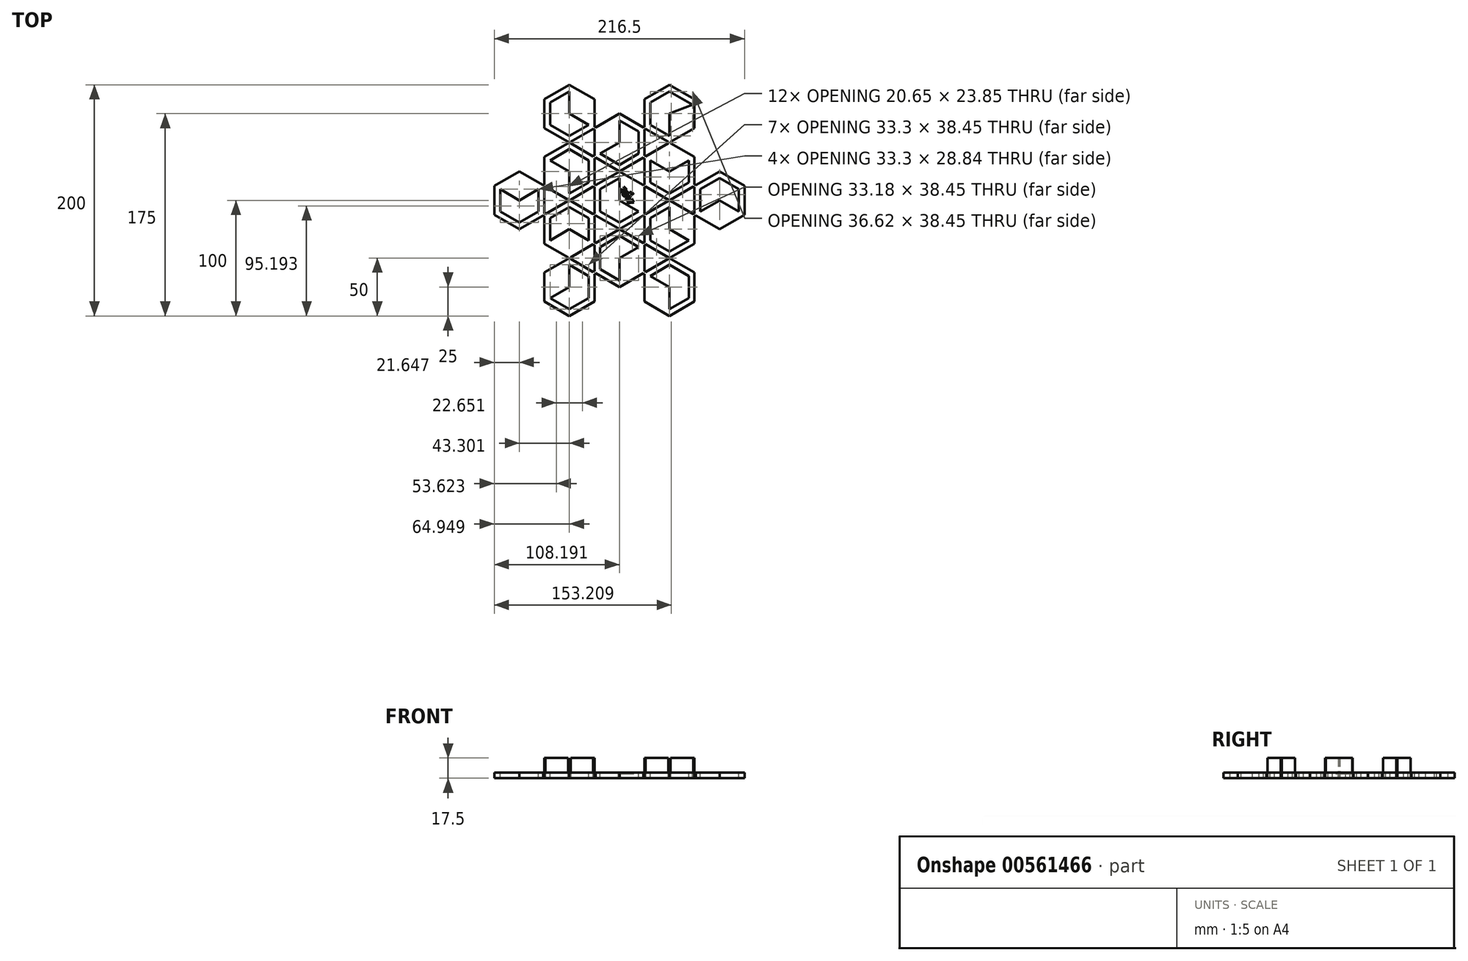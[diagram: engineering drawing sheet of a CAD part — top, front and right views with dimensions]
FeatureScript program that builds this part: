
annotation { "Feature Type Name" : "Feature", "Feature Type Description" : "" }
export const myFeature = defineFeature(function(context is Context, id is Id, definition is map)
    precondition{}
    {
        {
            var Q0;
            Q0=qCreatedBy(makeId("Top.planeOp"),FACE);
            var sketch = newSketch(context, id + "F0", { "sketchPlane" : qUnion([Q0])});
            skCircle(sketch, "E0.cCircle", {"center": v(0, 0) * mm, "radius": 25 * mm, "construction": true});
            skLineSegment(sketch, "E0.0", {"start": v(21.65, 12.5) * mm, "end": v(21.65, -12.5) * mm});
            skLineSegment(sketch, "E0.1", {"start": v(21.65, -12.5) * mm, "end": v(0, -25) * mm});
            skLineSegment(sketch, "E0.2", {"start": v(0, -25) * mm, "end": v(-21.65, -12.5) * mm});
            skLineSegment(sketch, "E0.3", {"start": v(-21.65, -12.5) * mm, "end": v(-21.65, 12.5) * mm});
            skLineSegment(sketch, "E0.4", {"start": v(-21.65, 12.5) * mm, "end": v(0, 25) * mm});
            skLineSegment(sketch, "E0.5", {"start": v(0, 25) * mm, "end": v(21.65, 12.5) * mm});
            skLineSegment(sketch, "E1.0", {"start": v(-16.65, 9.61) * mm, "end": v(0, 19.23) * mm});
            skLineSegment(sketch, "E1.1", {"start": v(-16.65, -9.61) * mm, "end": v(-16.65, 9.61) * mm});
            skLineSegment(sketch, "E1.2", {"start": v(0, -19.23) * mm, "end": v(-16.65, -9.61) * mm});
            skLineSegment(sketch, "E1.3", {"start": v(16.65, -9.61) * mm, "end": v(0, -19.23) * mm});
            skLineSegment(sketch, "E2", {"start": v(16.65, -9.61) * mm, "end": v(0, 0) * mm});
            skLineSegment(sketch, "E3", {"start": v(0, 19.23) * mm, "end": v(0, 0) * mm});
            skCircle(sketch, "E4.cCircle", {"center": v(0, -50) * mm, "radius": 25 * mm, "construction": true});
            skLineSegment(sketch, "E4.0", {"start": v(21.65, -62.5) * mm, "end": v(0, -75) * mm});
            skLineSegment(sketch, "E4.1", {"start": v(0, -75) * mm, "end": v(-21.65, -62.5) * mm});
            skLineSegment(sketch, "E4.2", {"start": v(-21.65, -62.5) * mm, "end": v(-21.65, -37.5) * mm});
            skLineSegment(sketch, "E4.3", {"start": v(-21.65, -37.5) * mm, "end": v(0, -25) * mm});
            skLineSegment(sketch, "E4.4", {"start": v(0, -25) * mm, "end": v(21.65, -37.5) * mm});
            skLineSegment(sketch, "E4.5", {"start": v(21.65, -37.5) * mm, "end": v(21.65, -62.5) * mm});
            skLineSegment(sketch, "E5.0", {"start": v(0, -30.77) * mm, "end": v(16.53, -40.32) * mm});
            skLineSegment(sketch, "E5.1", {"start": v(-16.65, -40.39) * mm, "end": v(0, -30.77) * mm});
            skLineSegment(sketch, "E5.2", {"start": v(-16.65, -59.61) * mm, "end": v(-16.65, -40.39) * mm});
            skLineSegment(sketch, "E5.3", {"start": v(0, -69.23) * mm, "end": v(-16.65, -59.61) * mm});
            skLineSegment(sketch, "E6", {"start": v(0, -69.23) * mm, "end": v(0, -50) * mm});
            skLineSegment(sketch, "E7", {"start": v(16.53, -40.32) * mm, "end": v(0, -50) * mm});
            skCircle(sketch, "E8.cCircle", {"center": v(-43.3, -25) * mm, "radius": 25 * mm, "construction": true});
            skLineSegment(sketch, "E8.0", {"start": v(-43.3, -50) * mm, "end": v(-64.95, -37.5) * mm});
            skLineSegment(sketch, "E8.1", {"start": v(-64.95, -37.5) * mm, "end": v(-64.95, -12.5) * mm});
            skLineSegment(sketch, "E8.2", {"start": v(-64.95, -12.5) * mm, "end": v(-43.3, 0) * mm});
            skLineSegment(sketch, "E8.3", {"start": v(-43.3, 0) * mm, "end": v(-21.65, -12.5) * mm});
            skLineSegment(sketch, "E8.4", {"start": v(-21.65, -12.5) * mm, "end": v(-21.65, -37.5) * mm});
            skLineSegment(sketch, "E8.5", {"start": v(-21.65, -37.5) * mm, "end": v(-43.3, -50) * mm});
            skLineSegment(sketch, "E9.0", {"start": v(-26.65, -15.39) * mm, "end": v(-26.65, -34.61) * mm});
            skLineSegment(sketch, "E9.1", {"start": v(-43.3, -5.77) * mm, "end": v(-26.65, -15.39) * mm});
            skLineSegment(sketch, "E9.2", {"start": v(-59.95, -15.39) * mm, "end": v(-43.3, -5.77) * mm});
            skLineSegment(sketch, "E9.3", {"start": v(-59.95, -34.61) * mm, "end": v(-59.95, -15.39) * mm});
            skLineSegment(sketch, "E10", {"start": v(-59.95, -34.61) * mm, "end": v(-43.3, -25) * mm});
            skLineSegment(sketch, "E11", {"start": v(-26.65, -34.61) * mm, "end": v(-43.3, -25) * mm});
            skCircle(sketch, "E12.cCircle", {"center": v(-43.3, 25) * mm, "radius": 25 * mm, "construction": true});
            skLineSegment(sketch, "E12.0", {"start": v(-64.95, 12.5) * mm, "end": v(-64.95, 37.5) * mm});
            skLineSegment(sketch, "E12.1", {"start": v(-64.95, 37.5) * mm, "end": v(-43.3, 50) * mm});
            skLineSegment(sketch, "E12.2", {"start": v(-43.3, 50) * mm, "end": v(-21.65, 37.5) * mm});
            skLineSegment(sketch, "E12.3", {"start": v(-21.65, 37.5) * mm, "end": v(-21.65, 12.5) * mm});
            skLineSegment(sketch, "E12.4", {"start": v(-21.65, 12.5) * mm, "end": v(-43.3, 0) * mm});
            skLineSegment(sketch, "E12.5", {"start": v(-43.3, 0) * mm, "end": v(-64.95, 12.5) * mm});
            skLineSegment(sketch, "E13.0", {"start": v(-26.65, 15.39) * mm, "end": v(-43.3, 5.77) * mm});
            skLineSegment(sketch, "E13.1", {"start": v(-26.65, 34.61) * mm, "end": v(-26.65, 15.39) * mm});
            skLineSegment(sketch, "E13.2", {"start": v(-43.3, 44.23) * mm, "end": v(-26.65, 34.61) * mm});
            skLineSegment(sketch, "E13.3", {"start": v(-59.95, 34.61) * mm, "end": v(-43.3, 44.23) * mm});
            skLineSegment(sketch, "E14", {"start": v(-59.95, 34.61) * mm, "end": v(-43.3, 25) * mm});
            skLineSegment(sketch, "E15", {"start": v(-43.3, 5.77) * mm, "end": v(-43.3, 25) * mm});
            skCircle(sketch, "E16.cCircle", {"center": v(0, 50) * mm, "radius": 25 * mm, "construction": true});
            skLineSegment(sketch, "E16.0", {"start": v(-21.65, 62.5) * mm, "end": v(0, 75) * mm});
            skLineSegment(sketch, "E16.1", {"start": v(0, 75) * mm, "end": v(21.65, 62.5) * mm});
            skLineSegment(sketch, "E16.2", {"start": v(21.65, 62.5) * mm, "end": v(21.65, 37.5) * mm});
            skLineSegment(sketch, "E16.3", {"start": v(21.65, 37.5) * mm, "end": v(0, 25) * mm});
            skLineSegment(sketch, "E16.4", {"start": v(0, 25) * mm, "end": v(-21.65, 37.5) * mm});
            skLineSegment(sketch, "E16.5", {"start": v(-21.65, 37.5) * mm, "end": v(-21.65, 62.5) * mm});
            skLineSegment(sketch, "E17.0", {"start": v(0, 30.77) * mm, "end": v(-16.65, 40.39) * mm});
            skLineSegment(sketch, "E17.1", {"start": v(16.65, 40.39) * mm, "end": v(0, 30.77) * mm});
            skLineSegment(sketch, "E17.2", {"start": v(16.65, 59.61) * mm, "end": v(16.65, 40.39) * mm});
            skLineSegment(sketch, "E17.3", {"start": v(0, 69.23) * mm, "end": v(16.65, 59.61) * mm});
            skLineSegment(sketch, "E18", {"start": v(0, 69.23) * mm, "end": v(0, 50) * mm});
            skLineSegment(sketch, "E19", {"start": v(-16.65, 40.39) * mm, "end": v(0, 50) * mm});
            skCircle(sketch, "E20.cCircle", {"center": v(43.3, 25) * mm, "radius": 25 * mm, "construction": true});
            skLineSegment(sketch, "E20.0", {"start": v(64.95, 12.5) * mm, "end": v(43.3, 0) * mm});
            skLineSegment(sketch, "E20.1", {"start": v(43.3, 0) * mm, "end": v(21.65, 12.5) * mm});
            skLineSegment(sketch, "E20.2", {"start": v(21.65, 12.5) * mm, "end": v(21.65, 37.5) * mm});
            skLineSegment(sketch, "E20.3", {"start": v(21.65, 37.5) * mm, "end": v(43.3, 50) * mm});
            skLineSegment(sketch, "E20.4", {"start": v(43.3, 50) * mm, "end": v(64.95, 37.5) * mm});
            skLineSegment(sketch, "E20.5", {"start": v(64.95, 37.5) * mm, "end": v(64.95, 12.5) * mm});
            skCircle(sketch, "E21.cCircle", {"center": v(43.3, -25) * mm, "radius": 25 * mm, "construction": true});
            skLineSegment(sketch, "E21.0", {"start": v(43.3, -50) * mm, "end": v(21.65, -37.5) * mm});
            skLineSegment(sketch, "E21.1", {"start": v(21.65, -37.5) * mm, "end": v(21.65, -12.5) * mm});
            skLineSegment(sketch, "E21.2", {"start": v(21.65, -12.5) * mm, "end": v(43.3, 0) * mm});
            skLineSegment(sketch, "E21.3", {"start": v(43.3, 0) * mm, "end": v(64.95, -12.5) * mm});
            skLineSegment(sketch, "E21.4", {"start": v(64.95, -12.5) * mm, "end": v(64.95, -37.5) * mm});
            skLineSegment(sketch, "E21.5", {"start": v(64.95, -37.5) * mm, "end": v(43.3, -50) * mm});
            skCircle(sketch, "E22.cCircle", {"center": v(-86.6, 0) * mm, "radius": 25 * mm, "construction": true});
            skLineSegment(sketch, "E22.0", {"start": v(-86.6, 25) * mm, "end": v(-64.95, 12.5) * mm});
            skLineSegment(sketch, "E22.1", {"start": v(-64.95, 12.5) * mm, "end": v(-64.95, -12.5) * mm});
            skLineSegment(sketch, "E22.2", {"start": v(-64.95, -12.5) * mm, "end": v(-86.6, -25) * mm});
            skLineSegment(sketch, "E22.3", {"start": v(-86.6, -25) * mm, "end": v(-108.25, -12.5) * mm});
            skLineSegment(sketch, "E22.4", {"start": v(-108.25, -12.5) * mm, "end": v(-108.25, 12.5) * mm});
            skLineSegment(sketch, "E22.5", {"start": v(-108.25, 12.5) * mm, "end": v(-86.6, 25) * mm});
            skLineSegment(sketch, "E23.0", {"start": v(-103.25, -9.61) * mm, "end": v(-103.25, 9.61) * mm});
            skLineSegment(sketch, "E23.1", {"start": v(-86.6, -19.23) * mm, "end": v(-103.25, -9.61) * mm});
            skLineSegment(sketch, "E23.2", {"start": v(-69.95, -9.61) * mm, "end": v(-86.6, -19.23) * mm});
            skLineSegment(sketch, "E23.3", {"start": v(-69.95, 9.61) * mm, "end": v(-69.95, -9.61) * mm});
            skLineSegment(sketch, "E24", {"start": v(-69.95, 9.61) * mm, "end": v(-86.6, 0) * mm});
            skLineSegment(sketch, "E25", {"start": v(-103.25, 9.61) * mm, "end": v(-86.6, 0) * mm});
            skCircle(sketch, "E26.cCircle", {"center": v(-43.3, 75) * mm, "radius": 25 * mm, "construction": true});
            skLineSegment(sketch, "E26.0", {"start": v(-21.65, 87.5) * mm, "end": v(-21.65, 62.5) * mm});
            skLineSegment(sketch, "E26.1", {"start": v(-21.65, 62.5) * mm, "end": v(-43.3, 50) * mm});
            skLineSegment(sketch, "E26.2", {"start": v(-43.3, 50) * mm, "end": v(-64.95, 62.5) * mm});
            skLineSegment(sketch, "E26.3", {"start": v(-64.95, 62.5) * mm, "end": v(-64.95, 87.5) * mm});
            skLineSegment(sketch, "E26.4", {"start": v(-64.95, 87.5) * mm, "end": v(-43.3, 100) * mm});
            skLineSegment(sketch, "E26.5", {"start": v(-43.3, 100) * mm, "end": v(-21.65, 87.5) * mm});
            skLineSegment(sketch, "E27.0", {"start": v(-59.95, 84.61) * mm, "end": v(-43.3, 94.23) * mm});
            skLineSegment(sketch, "E27.1", {"start": v(-59.95, 65.39) * mm, "end": v(-59.95, 84.61) * mm});
            skLineSegment(sketch, "E27.2", {"start": v(-43.3, 55.77) * mm, "end": v(-59.95, 65.39) * mm});
            skLineSegment(sketch, "E27.3", {"start": v(-26.65, 65.39) * mm, "end": v(-43.3, 55.77) * mm});
            skLineSegment(sketch, "E28", {"start": v(-26.65, 65.39) * mm, "end": v(-43.3, 75) * mm});
            skLineSegment(sketch, "E29", {"start": v(-43.3, 94.23) * mm, "end": v(-43.3, 75) * mm});
            skCircle(sketch, "E30.cCircle", {"center": v(43.3, 75) * mm, "radius": 25 * mm, "construction": true});
            skLineSegment(sketch, "E30.0", {"start": v(64.95, 62.5) * mm, "end": v(43.3, 50) * mm});
            skLineSegment(sketch, "E30.1", {"start": v(43.3, 50) * mm, "end": v(21.65, 62.5) * mm});
            skLineSegment(sketch, "E30.2", {"start": v(21.65, 62.5) * mm, "end": v(21.65, 87.5) * mm});
            skLineSegment(sketch, "E30.3", {"start": v(21.65, 87.5) * mm, "end": v(43.3, 100) * mm});
            skLineSegment(sketch, "E30.4", {"start": v(43.3, 100) * mm, "end": v(64.95, 87.5) * mm});
            skLineSegment(sketch, "E30.5", {"start": v(64.95, 87.5) * mm, "end": v(64.95, 62.5) * mm});
            skLineSegment(sketch, "E31.0", {"start": v(43.3, 94.23) * mm, "end": v(63.27, 82.7) * mm});
            skLineSegment(sketch, "E31.1", {"start": v(26.65, 84.61) * mm, "end": v(43.3, 94.23) * mm});
            skLineSegment(sketch, "E31.2", {"start": v(26.65, 65.39) * mm, "end": v(26.65, 84.61) * mm});
            skLineSegment(sketch, "E31.3", {"start": v(43.3, 55.77) * mm, "end": v(26.65, 65.39) * mm});
            skLineSegment(sketch, "E32", {"start": v(43.3, 55.77) * mm, "end": v(43.3, 75) * mm});
            skLineSegment(sketch, "E33", {"start": v(63.27, 82.7) * mm, "end": v(43.3, 75) * mm});
            skCircle(sketch, "E34.cCircle", {"center": v(86.6, 0) * mm, "radius": 25 * mm, "construction": true});
            skLineSegment(sketch, "E34.0", {"start": v(86.6, -25) * mm, "end": v(64.95, -12.5) * mm});
            skLineSegment(sketch, "E34.1", {"start": v(64.95, -12.5) * mm, "end": v(64.95, 12.5) * mm});
            skLineSegment(sketch, "E34.2", {"start": v(64.95, 12.5) * mm, "end": v(86.6, 25) * mm});
            skLineSegment(sketch, "E34.3", {"start": v(86.6, 25) * mm, "end": v(108.25, 12.5) * mm});
            skLineSegment(sketch, "E34.4", {"start": v(108.25, 12.5) * mm, "end": v(108.25, -12.5) * mm});
            skLineSegment(sketch, "E34.5", {"start": v(108.25, -12.5) * mm, "end": v(86.6, -25) * mm});
            skLineSegment(sketch, "E35.0", {"start": v(103.25, 9.61) * mm, "end": v(103.25, -9.61) * mm});
            skLineSegment(sketch, "E35.1", {"start": v(86.6, 19.23) * mm, "end": v(103.25, 9.61) * mm});
            skLineSegment(sketch, "E35.2", {"start": v(69.95, 9.61) * mm, "end": v(86.6, 19.23) * mm});
            skLineSegment(sketch, "E35.3", {"start": v(69.95, -9.61) * mm, "end": v(69.95, 9.61) * mm});
            skLineSegment(sketch, "E36", {"start": v(69.95, -9.61) * mm, "end": v(86.6, 0) * mm});
            skLineSegment(sketch, "E37", {"start": v(103.25, -9.61) * mm, "end": v(86.6, 0) * mm});
            skCircle(sketch, "E38.cCircle", {"center": v(43.3, -75) * mm, "radius": 25 * mm, "construction": true});
            skLineSegment(sketch, "E38.0", {"start": v(21.65, -87.5) * mm, "end": v(21.65, -62.5) * mm});
            skLineSegment(sketch, "E38.1", {"start": v(21.65, -62.5) * mm, "end": v(43.3, -50) * mm});
            skLineSegment(sketch, "E38.2", {"start": v(43.3, -50) * mm, "end": v(64.95, -62.5) * mm});
            skLineSegment(sketch, "E38.3", {"start": v(64.95, -62.5) * mm, "end": v(64.95, -87.5) * mm});
            skLineSegment(sketch, "E38.4", {"start": v(64.95, -87.5) * mm, "end": v(43.3, -100) * mm});
            skLineSegment(sketch, "E38.5", {"start": v(43.3, -100) * mm, "end": v(21.65, -87.5) * mm});
            skLineSegment(sketch, "E39.0", {"start": v(59.95, -84.61) * mm, "end": v(43.3, -94.23) * mm});
            skLineSegment(sketch, "E39.1", {"start": v(59.95, -65.39) * mm, "end": v(59.95, -84.61) * mm});
            skLineSegment(sketch, "E39.2", {"start": v(43.3, -55.77) * mm, "end": v(59.95, -65.39) * mm});
            skLineSegment(sketch, "E39.3", {"start": v(26.65, -65.39) * mm, "end": v(43.3, -55.77) * mm});
            skLineSegment(sketch, "E40", {"start": v(26.65, -65.39) * mm, "end": v(43.3, -75) * mm});
            skLineSegment(sketch, "E41", {"start": v(43.3, -94.23) * mm, "end": v(43.3, -75) * mm});
            skCircle(sketch, "E42.cCircle", {"center": v(-43.3, -75) * mm, "radius": 25 * mm, "construction": true});
            skLineSegment(sketch, "E42.0", {"start": v(-64.95, -62.5) * mm, "end": v(-43.3, -50) * mm});
            skLineSegment(sketch, "E42.1", {"start": v(-43.3, -50) * mm, "end": v(-21.65, -62.5) * mm});
            skLineSegment(sketch, "E42.2", {"start": v(-21.65, -62.5) * mm, "end": v(-21.65, -87.5) * mm});
            skLineSegment(sketch, "E42.3", {"start": v(-21.65, -87.5) * mm, "end": v(-43.3, -100) * mm});
            skLineSegment(sketch, "E42.4", {"start": v(-43.3, -100) * mm, "end": v(-64.95, -87.5) * mm});
            skLineSegment(sketch, "E42.5", {"start": v(-64.95, -87.5) * mm, "end": v(-64.95, -62.5) * mm});
            skLineSegment(sketch, "E43.0", {"start": v(-43.3, -94.23) * mm, "end": v(-59.95, -84.61) * mm});
            skLineSegment(sketch, "E43.1", {"start": v(-26.65, -84.61) * mm, "end": v(-43.3, -94.23) * mm});
            skLineSegment(sketch, "E43.2", {"start": v(-26.65, -65.39) * mm, "end": v(-26.65, -84.61) * mm});
            skLineSegment(sketch, "E43.3", {"start": v(-43.3, -55.77) * mm, "end": v(-26.65, -65.39) * mm});
            skLineSegment(sketch, "E44", {"start": v(-43.3, -55.77) * mm, "end": v(-43.3, -75) * mm});
            skLineSegment(sketch, "E45", {"start": v(-59.95, -84.61) * mm, "end": v(-43.3, -75) * mm});
            skLineSegment(sketch, "E46.bottom", {"start": v(-20.65, -11.5) * mm, "end": v(-22.65, -11.5) * mm});
            skLineSegment(sketch, "E46.top", {"start": v(-20.65, -13.5) * mm, "end": v(-22.65, -13.5) * mm});
            skLineSegment(sketch, "E46.left", {"start": v(-20.65, -11.5) * mm, "end": v(-20.65, -13.5) * mm});
            skLineSegment(sketch, "E46.right", {"start": v(-22.65, -11.5) * mm, "end": v(-22.65, -13.5) * mm});
            skPoint(sketch, "E46.middle", {"position": v(-21.65, -12.5) * mm});
            skLineSegment(sketch, "E47.bottom", {"start": v(1, -24) * mm, "end": v(-1, -24) * mm});
            skLineSegment(sketch, "E47.top", {"start": v(1, -26) * mm, "end": v(-1, -26) * mm});
            skLineSegment(sketch, "E47.left", {"start": v(1, -24) * mm, "end": v(1, -26) * mm});
            skLineSegment(sketch, "E47.right", {"start": v(-1, -24) * mm, "end": v(-1, -26) * mm});
            skPoint(sketch, "E47.middle", {"position": v(0, -25) * mm});
            skLineSegment(sketch, "E48.bottom", {"start": v(20.65, -11.5) * mm, "end": v(22.65, -11.5) * mm});
            skLineSegment(sketch, "E48.top", {"start": v(20.65, -13.5) * mm, "end": v(22.65, -13.5) * mm});
            skLineSegment(sketch, "E48.left", {"start": v(20.65, -11.5) * mm, "end": v(20.65, -13.5) * mm});
            skLineSegment(sketch, "E48.right", {"start": v(22.65, -11.5) * mm, "end": v(22.65, -13.5) * mm});
            skPoint(sketch, "E48.middle", {"position": v(21.65, -12.5) * mm});
            skLineSegment(sketch, "E49.bottom", {"start": v(20.65, 11.5) * mm, "end": v(22.65, 11.5) * mm});
            skLineSegment(sketch, "E49.top", {"start": v(20.65, 13.5) * mm, "end": v(22.65, 13.5) * mm});
            skLineSegment(sketch, "E49.left", {"start": v(20.65, 11.5) * mm, "end": v(20.65, 13.5) * mm});
            skLineSegment(sketch, "E49.right", {"start": v(22.65, 11.5) * mm, "end": v(22.65, 13.5) * mm});
            skPoint(sketch, "E49.middle", {"position": v(21.65, 12.5) * mm});
            skLineSegment(sketch, "E50.bottom", {"start": v(-1, 24) * mm, "end": v(1, 24) * mm});
            skLineSegment(sketch, "E50.top", {"start": v(-1, 26) * mm, "end": v(1, 26) * mm});
            skLineSegment(sketch, "E50.left", {"start": v(-1, 24) * mm, "end": v(-1, 26) * mm});
            skLineSegment(sketch, "E50.right", {"start": v(1, 24) * mm, "end": v(1, 26) * mm});
            skPoint(sketch, "E50.middle", {"position": v(0, 25) * mm});
            skLineSegment(sketch, "E51.bottom", {"start": v(-20.65, 11.5) * mm, "end": v(-22.65, 11.5) * mm});
            skLineSegment(sketch, "E51.top", {"start": v(-20.65, 13.5) * mm, "end": v(-22.65, 13.5) * mm});
            skLineSegment(sketch, "E51.left", {"start": v(-20.65, 11.5) * mm, "end": v(-20.65, 13.5) * mm});
            skLineSegment(sketch, "E51.right", {"start": v(-22.65, 11.5) * mm, "end": v(-22.65, 13.5) * mm});
            skPoint(sketch, "E51.middle", {"position": v(-21.65, 12.5) * mm});
            skLineSegment(sketch, "E52.bottom", {"start": v(44.3, -1) * mm, "end": v(42.3, -1) * mm});
            skLineSegment(sketch, "E52.top", {"start": v(44.3, 1) * mm, "end": v(42.3, 1) * mm});
            skLineSegment(sketch, "E52.left", {"start": v(44.3, -1) * mm, "end": v(44.3, 1) * mm});
            skLineSegment(sketch, "E52.right", {"start": v(42.3, -1) * mm, "end": v(42.3, 1) * mm});
            skPoint(sketch, "E52.middle", {"position": v(43.3, 0) * mm});
            skLineSegment(sketch, "E53.bottom", {"start": v(20.65, 38.5) * mm, "end": v(22.65, 38.5) * mm});
            skLineSegment(sketch, "E53.top", {"start": v(20.65, 36.5) * mm, "end": v(22.65, 36.5) * mm});
            skLineSegment(sketch, "E53.left", {"start": v(20.65, 38.5) * mm, "end": v(20.65, 36.5) * mm});
            skLineSegment(sketch, "E53.right", {"start": v(22.65, 38.5) * mm, "end": v(22.65, 36.5) * mm});
            skPoint(sketch, "E53.middle", {"position": v(21.65, 37.5) * mm});
            skLineSegment(sketch, "E54.bottom", {"start": v(63.95, 13.5) * mm, "end": v(65.95, 13.5) * mm});
            skLineSegment(sketch, "E54.top", {"start": v(63.95, 11.5) * mm, "end": v(65.95, 11.5) * mm});
            skLineSegment(sketch, "E54.left", {"start": v(63.95, 13.5) * mm, "end": v(63.95, 11.5) * mm});
            skLineSegment(sketch, "E54.right", {"start": v(65.95, 13.5) * mm, "end": v(65.95, 11.5) * mm});
            skPoint(sketch, "E54.middle", {"position": v(64.95, 12.5) * mm});
            skLineSegment(sketch, "E55.bottom", {"start": v(-20.65, 38.5) * mm, "end": v(-22.65, 38.5) * mm});
            skLineSegment(sketch, "E55.top", {"start": v(-20.65, 36.5) * mm, "end": v(-22.65, 36.5) * mm});
            skLineSegment(sketch, "E55.left", {"start": v(-20.65, 38.5) * mm, "end": v(-20.65, 36.5) * mm});
            skLineSegment(sketch, "E55.right", {"start": v(-22.65, 38.5) * mm, "end": v(-22.65, 36.5) * mm});
            skPoint(sketch, "E55.middle", {"position": v(-21.65, 37.5) * mm});
            skLineSegment(sketch, "E56.bottom", {"start": v(-42.3, 1) * mm, "end": v(-44.3, 1) * mm});
            skLineSegment(sketch, "E56.top", {"start": v(-42.3, -1) * mm, "end": v(-44.3, -1) * mm});
            skLineSegment(sketch, "E56.left", {"start": v(-42.3, 1) * mm, "end": v(-42.3, -1) * mm});
            skLineSegment(sketch, "E56.right", {"start": v(-44.3, 1) * mm, "end": v(-44.3, -1) * mm});
            skPoint(sketch, "E56.middle", {"position": v(-43.3, 0) * mm});
            skLineSegment(sketch, "E57.bottom", {"start": v(65.95, -11.5) * mm, "end": v(63.95, -11.5) * mm});
            skLineSegment(sketch, "E57.top", {"start": v(65.95, -13.5) * mm, "end": v(63.95, -13.5) * mm});
            skLineSegment(sketch, "E57.left", {"start": v(65.95, -11.5) * mm, "end": v(65.95, -13.5) * mm});
            skLineSegment(sketch, "E57.right", {"start": v(63.95, -11.5) * mm, "end": v(63.95, -13.5) * mm});
            skPoint(sketch, "E57.middle", {"position": v(64.95, -12.5) * mm});
            skLineSegment(sketch, "E58.bottom", {"start": v(44.3, -49) * mm, "end": v(42.3, -49) * mm});
            skLineSegment(sketch, "E58.top", {"start": v(44.3, -51) * mm, "end": v(42.3, -51) * mm});
            skLineSegment(sketch, "E58.left", {"start": v(44.3, -49) * mm, "end": v(44.3, -51) * mm});
            skLineSegment(sketch, "E58.right", {"start": v(42.3, -49) * mm, "end": v(42.3, -51) * mm});
            skPoint(sketch, "E58.middle", {"position": v(43.3, -50) * mm});
            skLineSegment(sketch, "E59.bottom", {"start": v(-42.3, -49) * mm, "end": v(-44.3, -49) * mm});
            skLineSegment(sketch, "E59.top", {"start": v(-42.3, -51) * mm, "end": v(-44.3, -51) * mm});
            skLineSegment(sketch, "E59.left", {"start": v(-42.3, -49) * mm, "end": v(-42.3, -51) * mm});
            skLineSegment(sketch, "E59.right", {"start": v(-44.3, -49) * mm, "end": v(-44.3, -51) * mm});
            skPoint(sketch, "E59.middle", {"position": v(-43.3, -50) * mm});
            skLineSegment(sketch, "E60.bottom", {"start": v(-63.95, -13.5) * mm, "end": v(-65.95, -13.5) * mm});
            skLineSegment(sketch, "E60.top", {"start": v(-63.95, -11.5) * mm, "end": v(-65.95, -11.5) * mm});
            skLineSegment(sketch, "E60.left", {"start": v(-63.95, -13.5) * mm, "end": v(-63.95, -11.5) * mm});
            skLineSegment(sketch, "E60.right", {"start": v(-65.95, -13.5) * mm, "end": v(-65.95, -11.5) * mm});
            skPoint(sketch, "E60.middle", {"position": v(-64.95, -12.5) * mm});
            skLineSegment(sketch, "E61.bottom", {"start": v(-63.95, 13.5) * mm, "end": v(-65.95, 13.5) * mm});
            skLineSegment(sketch, "E61.top", {"start": v(-63.95, 11.5) * mm, "end": v(-65.95, 11.5) * mm});
            skLineSegment(sketch, "E61.left", {"start": v(-63.95, 13.5) * mm, "end": v(-63.95, 11.5) * mm});
            skLineSegment(sketch, "E61.right", {"start": v(-65.95, 13.5) * mm, "end": v(-65.95, 11.5) * mm});
            skPoint(sketch, "E61.middle", {"position": v(-64.95, 12.5) * mm});
            skLineSegment(sketch, "E62.bottom", {"start": v(-42.3, 51) * mm, "end": v(-44.3, 51) * mm});
            skLineSegment(sketch, "E62.top", {"start": v(-42.3, 49) * mm, "end": v(-44.3, 49) * mm});
            skLineSegment(sketch, "E62.left", {"start": v(-42.3, 51) * mm, "end": v(-42.3, 49) * mm});
            skLineSegment(sketch, "E62.right", {"start": v(-44.3, 51) * mm, "end": v(-44.3, 49) * mm});
            skPoint(sketch, "E62.middle", {"position": v(-43.3, 50) * mm});
            skLineSegment(sketch, "E63.bottom", {"start": v(-22.65, 63.5) * mm, "end": v(-20.65, 63.5) * mm});
            skLineSegment(sketch, "E63.top", {"start": v(-22.65, 61.5) * mm, "end": v(-20.65, 61.5) * mm});
            skLineSegment(sketch, "E63.left", {"start": v(-22.65, 63.5) * mm, "end": v(-22.65, 61.5) * mm});
            skLineSegment(sketch, "E63.right", {"start": v(-20.65, 63.5) * mm, "end": v(-20.65, 61.5) * mm});
            skPoint(sketch, "E63.middle", {"position": v(-21.65, 62.5) * mm});
            skLineSegment(sketch, "E64.bottom", {"start": v(22.65, 63.5) * mm, "end": v(20.65, 63.5) * mm});
            skLineSegment(sketch, "E64.top", {"start": v(22.65, 61.5) * mm, "end": v(20.65, 61.5) * mm});
            skLineSegment(sketch, "E64.left", {"start": v(22.65, 63.5) * mm, "end": v(22.65, 61.5) * mm});
            skLineSegment(sketch, "E64.right", {"start": v(20.65, 63.5) * mm, "end": v(20.65, 61.5) * mm});
            skPoint(sketch, "E64.middle", {"position": v(21.65, 62.5) * mm});
            skLineSegment(sketch, "E65.bottom", {"start": v(44.3, 51) * mm, "end": v(42.3, 51) * mm});
            skLineSegment(sketch, "E65.top", {"start": v(44.3, 49) * mm, "end": v(42.3, 49) * mm});
            skLineSegment(sketch, "E65.left", {"start": v(44.3, 51) * mm, "end": v(44.3, 49) * mm});
            skLineSegment(sketch, "E65.right", {"start": v(42.3, 51) * mm, "end": v(42.3, 49) * mm});
            skPoint(sketch, "E65.middle", {"position": v(43.3, 50) * mm});
            skLineSegment(sketch, "E66.bottom", {"start": v(-20.65, -61.5) * mm, "end": v(-22.65, -61.5) * mm});
            skLineSegment(sketch, "E66.top", {"start": v(-20.65, -63.5) * mm, "end": v(-22.65, -63.5) * mm});
            skLineSegment(sketch, "E66.left", {"start": v(-20.65, -61.5) * mm, "end": v(-20.65, -63.5) * mm});
            skLineSegment(sketch, "E66.right", {"start": v(-22.65, -61.5) * mm, "end": v(-22.65, -63.5) * mm});
            skPoint(sketch, "E66.middle", {"position": v(-21.65, -62.5) * mm});
            skLineSegment(sketch, "E67.bottom", {"start": v(-22.65, -36.5) * mm, "end": v(-20.65, -36.5) * mm});
            skLineSegment(sketch, "E67.top", {"start": v(-22.65, -38.5) * mm, "end": v(-20.65, -38.5) * mm});
            skLineSegment(sketch, "E67.left", {"start": v(-22.65, -36.5) * mm, "end": v(-22.65, -38.5) * mm});
            skLineSegment(sketch, "E67.right", {"start": v(-20.65, -36.5) * mm, "end": v(-20.65, -38.5) * mm});
            skPoint(sketch, "E67.middle", {"position": v(-21.65, -37.5) * mm});
            skLineSegment(sketch, "E68.bottom", {"start": v(22.65, -36.5) * mm, "end": v(20.65, -36.5) * mm});
            skLineSegment(sketch, "E68.top", {"start": v(22.65, -38.5) * mm, "end": v(20.65, -38.5) * mm});
            skLineSegment(sketch, "E68.left", {"start": v(22.65, -36.5) * mm, "end": v(22.65, -38.5) * mm});
            skLineSegment(sketch, "E68.right", {"start": v(20.65, -36.5) * mm, "end": v(20.65, -38.5) * mm});
            skPoint(sketch, "E68.middle", {"position": v(21.65, -37.5) * mm});
            skLineSegment(sketch, "E69.bottom", {"start": v(20.65, -61.5) * mm, "end": v(22.65, -61.5) * mm});
            skLineSegment(sketch, "E69.top", {"start": v(20.65, -63.5) * mm, "end": v(22.65, -63.5) * mm});
            skLineSegment(sketch, "E69.left", {"start": v(20.65, -61.5) * mm, "end": v(20.65, -63.5) * mm});
            skLineSegment(sketch, "E69.right", {"start": v(22.65, -61.5) * mm, "end": v(22.65, -63.5) * mm});
            skPoint(sketch, "E69.middle", {"position": v(21.65, -62.5) * mm});
            skLineSegment(sketch, "E70.0", {"start": v(26.65, -15.39) * mm, "end": v(43.3, -5.77) * mm});
            skLineSegment(sketch, "E70.1", {"start": v(26.65, -34.61) * mm, "end": v(26.65, -15.39) * mm});
            skLineSegment(sketch, "E70.2", {"start": v(43.3, -44.23) * mm, "end": v(26.65, -34.61) * mm});
            skLineSegment(sketch, "E70.3", {"start": v(59.95, -34.61) * mm, "end": v(43.3, -44.23) * mm});
            skPoint(sketch, "E71.endSnap0", {"position": v(43.3, -1) * mm});
            skLineSegment(sketch, "E72", {"start": v(59.95, -34.61) * mm, "end": v(43.3, -25) * mm});
            skLineSegment(sketch, "E73", {"start": v(43.3, -5.77) * mm, "end": v(43.3, -25) * mm});
            skLineSegment(sketch, "E74.0", {"start": v(26.65, 15.39) * mm, "end": v(26.65, 34.61) * mm});
            skLineSegment(sketch, "E74.1", {"start": v(43.3, 5.77) * mm, "end": v(26.65, 15.39) * mm});
            skLineSegment(sketch, "E74.2", {"start": v(59.95, 15.39) * mm, "end": v(43.3, 5.77) * mm});
            skLineSegment(sketch, "E74.3", {"start": v(59.95, 34.61) * mm, "end": v(59.95, 15.39) * mm});
            skLineSegment(sketch, "E75", {"start": v(59.95, 34.61) * mm, "end": v(43.3, 25) * mm});
            skLineSegment(sketch, "E76.trimOffspring", {"start": v(26.65, 34.61) * mm, "end": v(43.3, 25) * mm});
            skSolve(sketch);
        }
        {
            var Q0;
            Q0=makeQuery(id+"F0.imprint","IMPRINT",FACE,{"disambiguationData":[TD([[makeQuery(id+"F0.imprint","IMPRINT",EDGE,{"derivedFrom":sQuery(id+"F0.wireOp",EDGE,"E13.0")}),1.0]])]});
            var Q1;
            {var subQ1=sQuery(id+"F0.wireOp",EDGE,"E62.top");Q1=makeQuery(id+"F0.imprint","IMPRINT",FACE,{"disambiguationData":[TD([[makeQuery(id+"F0.imprint","IMPRINT",EDGE,{"derivedFrom":subQ1}),-1.0]])]});}
            var Q2;
            {var subQ1=sQuery(id+"F0.wireOp",EDGE,"E12.1");var subQ3=sQuery(id+"F0.wireOp",EDGE,"E62.right");var subQ4=makeQuery(id+"F0.imprint","INTERSECT",VERTEX,{"derivedFrom":[subQ1,subQ3]});Q2=makeQuery(id+"F0.imprint","IMPRINT",FACE,{"disambiguationData":[TD([[makeQuery(id+"F0.imprint","IMPRINT",EDGE,{"disambiguationData":[TD([[subQ4,1.0]])],"derivedFrom":subQ3}),1.0]])]});}
            var Q3;
            {var subQ0=sQuery(id+"F0.wireOp",EDGE,"E62.bottom");Q3=makeQuery(id+"F0.imprint","IMPRINT",FACE,{"disambiguationData":[TD([[makeQuery(id+"F0.imprint","IMPRINT",EDGE,{"derivedFrom":subQ0}),1.0]])]});}
            var Q4;
            {var subQ1=sQuery(id+"F0.wireOp",EDGE,"E12.2");var subQ3=sQuery(id+"F0.wireOp",EDGE,"E62.left");var subQ4=makeQuery(id+"F0.imprint","INTERSECT",VERTEX,{"derivedFrom":[subQ1,subQ3]});Q4=makeQuery(id+"F0.imprint","IMPRINT",FACE,{"disambiguationData":[TD([[makeQuery(id+"F0.imprint","IMPRINT",EDGE,{"disambiguationData":[TD([[subQ4,1.0]])],"derivedFrom":subQ3}),-1.0]])]});}
            var Q5;
            {var subQ11=sQuery(id+"F0.wireOp",EDGE,"E26.3");Q5=makeQuery(id+"F0.imprint","IMPRINT",FACE,{"disambiguationData":[TD([[makeQuery(id+"F0.imprint","IMPRINT",EDGE,{"derivedFrom":subQ11}),-1.0]])]});}
            var Q6;
            {var subQ3=sQuery(id+"F0.wireOp",EDGE,"E55.left");var subQ5=sQuery(id+"F0.wireOp",EDGE,"E55.bottom");var subQ7=makeQuery(id+"F0.imprint","INTERSECT",VERTEX,{"derivedFrom":[subQ5,subQ3]});Q6=makeQuery(id+"F0.imprint","IMPRINT",FACE,{"disambiguationData":[TD([[makeQuery(id+"F0.imprint","IMPRINT",EDGE,{"disambiguationData":[TD([[subQ7,-1.0]])],"derivedFrom":subQ5}),1.0]])]});}
            var Q7;
            Q7=makeQuery(id+"F0.imprint","IMPRINT",FACE,{"disambiguationData":[TD([[makeQuery(id+"F0.imprint","IMPRINT",EDGE,{"derivedFrom":sQuery(id+"F0.wireOp",EDGE,"E17.0")}),1.0]])]});
            var Q8;
            {var subQ3=sQuery(id+"F0.wireOp",EDGE,"E55.right");var subQ5=sQuery(id+"F0.wireOp",EDGE,"E55.top");var subQ7=makeQuery(id+"F0.imprint","INTERSECT",VERTEX,{"derivedFrom":[subQ5,subQ3]});Q8=makeQuery(id+"F0.imprint","IMPRINT",FACE,{"disambiguationData":[TD([[makeQuery(id+"F0.imprint","IMPRINT",EDGE,{"disambiguationData":[TD([[subQ7,1.0]])],"derivedFrom":subQ5}),-1.0]])]});}
            var Q9;
            {var subQ3=sQuery(id+"F0.wireOp",EDGE,"E55.top");var subQ5=sQuery(id+"F0.wireOp",EDGE,"E55.left");var subQ7=makeQuery(id+"F0.imprint","INTERSECT",VERTEX,{"derivedFrom":[subQ3,subQ5]});Q9=makeQuery(id+"F0.imprint","IMPRINT",FACE,{"disambiguationData":[TD([[makeQuery(id+"F0.imprint","IMPRINT",EDGE,{"disambiguationData":[TD([[subQ7,-1.0]])],"derivedFrom":subQ3}),-1.0]])]});}
            var Q10;
            {var subQ3=sQuery(id+"F0.wireOp",EDGE,"E55.right");var subQ5=sQuery(id+"F0.wireOp",EDGE,"E55.bottom");var subQ7=makeQuery(id+"F0.imprint","INTERSECT",VERTEX,{"derivedFrom":[subQ5,subQ3]});Q10=makeQuery(id+"F0.imprint","IMPRINT",FACE,{"disambiguationData":[TD([[makeQuery(id+"F0.imprint","IMPRINT",EDGE,{"disambiguationData":[TD([[subQ7,1.0]])],"derivedFrom":subQ5}),1.0]])]});}
            var Q11;
            Q11=makeQuery(id+"F0.imprint","IMPRINT",FACE,{"disambiguationData":[TD([[makeQuery(id+"F0.imprint","IMPRINT",EDGE,{"derivedFrom":sQuery(id+"F0.wireOp",EDGE,"E1.0")}),1.0]])]});
            var Q12;
            {var subQ1=sQuery(id+"F0.wireOp",EDGE,"E50.top");Q12=makeQuery(id+"F0.imprint","IMPRINT",FACE,{"disambiguationData":[TD([[makeQuery(id+"F0.imprint","IMPRINT",EDGE,{"derivedFrom":subQ1}),-1.0]])]});}
            var Q13;
            {var subQ1=sQuery(id+"F0.wireOp",EDGE,"E50.bottom");Q13=makeQuery(id+"F0.imprint","IMPRINT",FACE,{"disambiguationData":[TD([[makeQuery(id+"F0.imprint","IMPRINT",EDGE,{"derivedFrom":subQ1}),1.0]])]});}
            var Q14;
            {var subQ1=sQuery(id+"F0.wireOp",EDGE,"E50.bottom");Q14=makeQuery(id+"F0.imprint","IMPRINT",FACE,{"disambiguationData":[TD([[makeQuery(id+"F0.imprint","IMPRINT",EDGE,{"derivedFrom":subQ1}),1.0]])]});}
            var Q15;
            {var subQ1=sQuery(id+"F0.wireOp",EDGE,"E0.4");var subQ3=sQuery(id+"F0.wireOp",EDGE,"E50.left");var subQ4=makeQuery(id+"F0.imprint","INTERSECT",VERTEX,{"derivedFrom":[subQ1,subQ3]});Q15=makeQuery(id+"F0.imprint","IMPRINT",FACE,{"disambiguationData":[TD([[makeQuery(id+"F0.imprint","IMPRINT",EDGE,{"disambiguationData":[TD([[subQ4,-1.0]])],"derivedFrom":subQ3}),-1.0]])]});}
            var Q16;
            {var subQ1=sQuery(id+"F0.wireOp",EDGE,"E0.5");var subQ3=sQuery(id+"F0.wireOp",EDGE,"E50.right");var subQ4=makeQuery(id+"F0.imprint","INTERSECT",VERTEX,{"derivedFrom":[subQ1,subQ3]});Q16=makeQuery(id+"F0.imprint","IMPRINT",FACE,{"disambiguationData":[TD([[makeQuery(id+"F0.imprint","IMPRINT",EDGE,{"disambiguationData":[TD([[subQ4,-1.0]])],"derivedFrom":subQ3}),1.0]])]});}
            var Q17;
            {var subQ3=sQuery(id+"F0.wireOp",EDGE,"E51.left");var subQ5=sQuery(id+"F0.wireOp",EDGE,"E51.top");var subQ7=makeQuery(id+"F0.imprint","INTERSECT",VERTEX,{"derivedFrom":[subQ5,subQ3]});Q17=makeQuery(id+"F0.imprint","IMPRINT",FACE,{"disambiguationData":[TD([[makeQuery(id+"F0.imprint","IMPRINT",EDGE,{"disambiguationData":[TD([[subQ7,-1.0]])],"derivedFrom":subQ5}),1.0]])]});}
            var Q18;
            {var subQ3=sQuery(id+"F0.wireOp",EDGE,"E51.top");var subQ5=sQuery(id+"F0.wireOp",EDGE,"E51.right");var subQ7=makeQuery(id+"F0.imprint","INTERSECT",VERTEX,{"derivedFrom":[subQ3,subQ5]});Q18=makeQuery(id+"F0.imprint","IMPRINT",FACE,{"disambiguationData":[TD([[makeQuery(id+"F0.imprint","IMPRINT",EDGE,{"disambiguationData":[TD([[subQ7,1.0]])],"derivedFrom":subQ3}),1.0]])]});}
            var Q19;
            {var subQ3=sQuery(id+"F0.wireOp",EDGE,"E51.bottom");var subQ5=sQuery(id+"F0.wireOp",EDGE,"E51.left");var subQ6=makeQuery(id+"F0.imprint","INTERSECT",VERTEX,{"derivedFrom":[subQ3,subQ5]});Q19=makeQuery(id+"F0.imprint","IMPRINT",FACE,{"disambiguationData":[TD([[makeQuery(id+"F0.imprint","IMPRINT",EDGE,{"disambiguationData":[TD([[subQ6,-1.0]])],"derivedFrom":subQ3}),-1.0]])]});}
            var Q20;
            {var subQ3=sQuery(id+"F0.wireOp",EDGE,"E51.bottom");var subQ5=sQuery(id+"F0.wireOp",EDGE,"E51.right");var subQ7=makeQuery(id+"F0.imprint","INTERSECT",VERTEX,{"derivedFrom":[subQ3,subQ5]});Q20=makeQuery(id+"F0.imprint","IMPRINT",FACE,{"disambiguationData":[TD([[makeQuery(id+"F0.imprint","IMPRINT",EDGE,{"disambiguationData":[TD([[subQ7,1.0]])],"derivedFrom":subQ3}),-1.0]])]});}
            var Q21;
            Q21=makeQuery(id+"F0.imprint","IMPRINT",FACE,{"disambiguationData":[TD([[makeQuery(id+"F0.imprint","IMPRINT",EDGE,{"derivedFrom":sQuery(id+"F0.wireOp",EDGE,"128f1ca7-f536-43b7-be13-3e55e3ce3627.0")}),1.0]])]});
            var Q22;
            {var subQ3=sQuery(id+"F0.wireOp",EDGE,"E49.right");var subQ5=sQuery(id+"F0.wireOp",EDGE,"E49.top");var subQ7=makeQuery(id+"F0.imprint","INTERSECT",VERTEX,{"derivedFrom":[subQ5,subQ3]});Q22=makeQuery(id+"F0.imprint","IMPRINT",FACE,{"disambiguationData":[TD([[makeQuery(id+"F0.imprint","IMPRINT",EDGE,{"disambiguationData":[TD([[subQ7,1.0]])],"derivedFrom":subQ5}),-1.0]])]});}
            var Q23;
            {var subQ3=sQuery(id+"F0.wireOp",EDGE,"E49.bottom");var subQ5=sQuery(id+"F0.wireOp",EDGE,"E49.left");var subQ6=makeQuery(id+"F0.imprint","INTERSECT",VERTEX,{"derivedFrom":[subQ3,subQ5]});Q23=makeQuery(id+"F0.imprint","IMPRINT",FACE,{"disambiguationData":[TD([[makeQuery(id+"F0.imprint","IMPRINT",EDGE,{"disambiguationData":[TD([[subQ6,-1.0]])],"derivedFrom":subQ3}),1.0]])]});}
            var Q24;
            {var subQ3=sQuery(id+"F0.wireOp",EDGE,"E49.bottom");var subQ5=sQuery(id+"F0.wireOp",EDGE,"E49.right");var subQ7=makeQuery(id+"F0.imprint","INTERSECT",VERTEX,{"derivedFrom":[subQ3,subQ5]});Q24=makeQuery(id+"F0.imprint","IMPRINT",FACE,{"disambiguationData":[TD([[makeQuery(id+"F0.imprint","IMPRINT",EDGE,{"disambiguationData":[TD([[subQ7,1.0]])],"derivedFrom":subQ3}),1.0]])]});}
            var Q25;
            {var subQ3=sQuery(id+"F0.wireOp",EDGE,"E49.left");var subQ5=sQuery(id+"F0.wireOp",EDGE,"E49.top");var subQ7=makeQuery(id+"F0.imprint","INTERSECT",VERTEX,{"derivedFrom":[subQ5,subQ3]});Q25=makeQuery(id+"F0.imprint","IMPRINT",FACE,{"disambiguationData":[TD([[makeQuery(id+"F0.imprint","IMPRINT",EDGE,{"disambiguationData":[TD([[subQ7,-1.0]])],"derivedFrom":subQ5}),-1.0]])]});}
            var Q26;
            {var subQ3=sQuery(id+"F0.wireOp",EDGE,"E53.top");var subQ5=sQuery(id+"F0.wireOp",EDGE,"E53.right");var subQ6=makeQuery(id+"F0.imprint","INTERSECT",VERTEX,{"derivedFrom":[subQ3,subQ5]});Q26=makeQuery(id+"F0.imprint","IMPRINT",FACE,{"disambiguationData":[TD([[makeQuery(id+"F0.imprint","IMPRINT",EDGE,{"disambiguationData":[TD([[subQ6,1.0]])],"derivedFrom":subQ3}),1.0]])]});}
            var Q27;
            {var subQ3=sQuery(id+"F0.wireOp",EDGE,"E53.bottom");var subQ5=sQuery(id+"F0.wireOp",EDGE,"E53.right");var subQ7=makeQuery(id+"F0.imprint","INTERSECT",VERTEX,{"derivedFrom":[subQ3,subQ5]});Q27=makeQuery(id+"F0.imprint","IMPRINT",FACE,{"disambiguationData":[TD([[makeQuery(id+"F0.imprint","IMPRINT",EDGE,{"disambiguationData":[TD([[subQ7,1.0]])],"derivedFrom":subQ3}),-1.0]])]});}
            var Q28;
            {var subQ3=sQuery(id+"F0.wireOp",EDGE,"E53.bottom");var subQ5=sQuery(id+"F0.wireOp",EDGE,"E53.left");var subQ7=makeQuery(id+"F0.imprint","INTERSECT",VERTEX,{"derivedFrom":[subQ3,subQ5]});Q28=makeQuery(id+"F0.imprint","IMPRINT",FACE,{"disambiguationData":[TD([[makeQuery(id+"F0.imprint","IMPRINT",EDGE,{"disambiguationData":[TD([[subQ7,-1.0]])],"derivedFrom":subQ3}),-1.0]])]});}
            var Q29;
            {var subQ3=sQuery(id+"F0.wireOp",EDGE,"E53.left");var subQ5=sQuery(id+"F0.wireOp",EDGE,"E53.top");var subQ7=makeQuery(id+"F0.imprint","INTERSECT",VERTEX,{"derivedFrom":[subQ5,subQ3]});Q29=makeQuery(id+"F0.imprint","IMPRINT",FACE,{"disambiguationData":[TD([[makeQuery(id+"F0.imprint","IMPRINT",EDGE,{"disambiguationData":[TD([[subQ7,-1.0]])],"derivedFrom":subQ5}),1.0]])]});}
            var Q30;
            {var subQ0=sQuery(id+"F0.wireOp",EDGE,"E65.top");Q30=makeQuery(id+"F0.imprint","IMPRINT",FACE,{"disambiguationData":[TD([[makeQuery(id+"F0.imprint","IMPRINT",EDGE,{"derivedFrom":subQ0}),-1.0]])]});}
            var Q31;
            {var subQ1=sQuery(id+"F0.wireOp",EDGE,"E20.4");var subQ3=sQuery(id+"F0.wireOp",EDGE,"E65.left");var subQ4=makeQuery(id+"F0.imprint","INTERSECT",VERTEX,{"derivedFrom":[subQ1,subQ3]});Q31=makeQuery(id+"F0.imprint","IMPRINT",FACE,{"disambiguationData":[TD([[makeQuery(id+"F0.imprint","IMPRINT",EDGE,{"disambiguationData":[TD([[subQ4,1.0]])],"derivedFrom":subQ3}),-1.0]])]});}
            var Q32;
            {var subQ1=sQuery(id+"F0.wireOp",EDGE,"E65.bottom");Q32=makeQuery(id+"F0.imprint","IMPRINT",FACE,{"disambiguationData":[TD([[makeQuery(id+"F0.imprint","IMPRINT",EDGE,{"derivedFrom":subQ1}),1.0]])]});}
            var Q33;
            {var subQ1=sQuery(id+"F0.wireOp",EDGE,"E20.3");var subQ3=sQuery(id+"F0.wireOp",EDGE,"E65.right");var subQ4=makeQuery(id+"F0.imprint","INTERSECT",VERTEX,{"derivedFrom":[subQ1,subQ3]});Q33=makeQuery(id+"F0.imprint","IMPRINT",FACE,{"disambiguationData":[TD([[makeQuery(id+"F0.imprint","IMPRINT",EDGE,{"disambiguationData":[TD([[subQ4,1.0]])],"derivedFrom":subQ3}),1.0]])]});}
            var Q34;
            {var subQ10=sQuery(id+"F0.wireOp",EDGE,"E30.3");Q34=makeQuery(id+"F0.imprint","IMPRINT",FACE,{"disambiguationData":[TD([[makeQuery(id+"F0.imprint","IMPRINT",EDGE,{"derivedFrom":subQ10}),-1.0]])]});}
            var Q35;
            {var subQ3=sQuery(id+"F0.wireOp",EDGE,"E64.left");var subQ5=sQuery(id+"F0.wireOp",EDGE,"E64.bottom");var subQ7=makeQuery(id+"F0.imprint","INTERSECT",VERTEX,{"derivedFrom":[subQ5,subQ3]});Q35=makeQuery(id+"F0.imprint","IMPRINT",FACE,{"disambiguationData":[TD([[makeQuery(id+"F0.imprint","IMPRINT",EDGE,{"disambiguationData":[TD([[subQ7,-1.0]])],"derivedFrom":subQ5}),1.0]])]});}
            var Q36;
            {var subQ3=sQuery(id+"F0.wireOp",EDGE,"E64.right");var subQ5=sQuery(id+"F0.wireOp",EDGE,"E64.bottom");var subQ7=makeQuery(id+"F0.imprint","INTERSECT",VERTEX,{"derivedFrom":[subQ5,subQ3]});Q36=makeQuery(id+"F0.imprint","IMPRINT",FACE,{"disambiguationData":[TD([[makeQuery(id+"F0.imprint","IMPRINT",EDGE,{"disambiguationData":[TD([[subQ7,1.0]])],"derivedFrom":subQ5}),1.0]])]});}
            var Q37;
            {var subQ3=sQuery(id+"F0.wireOp",EDGE,"E64.right");var subQ5=sQuery(id+"F0.wireOp",EDGE,"E64.top");var subQ6=makeQuery(id+"F0.imprint","INTERSECT",VERTEX,{"derivedFrom":[subQ5,subQ3]});Q37=makeQuery(id+"F0.imprint","IMPRINT",FACE,{"disambiguationData":[TD([[makeQuery(id+"F0.imprint","IMPRINT",EDGE,{"disambiguationData":[TD([[subQ6,1.0]])],"derivedFrom":subQ5}),-1.0]])]});}
            var Q38;
            {var subQ3=sQuery(id+"F0.wireOp",EDGE,"E64.top");var subQ5=sQuery(id+"F0.wireOp",EDGE,"E64.left");var subQ7=makeQuery(id+"F0.imprint","INTERSECT",VERTEX,{"derivedFrom":[subQ3,subQ5]});Q38=makeQuery(id+"F0.imprint","IMPRINT",FACE,{"disambiguationData":[TD([[makeQuery(id+"F0.imprint","IMPRINT",EDGE,{"disambiguationData":[TD([[subQ7,-1.0]])],"derivedFrom":subQ3}),-1.0]])]});}
            var Q39;
            {var subQ11=sQuery(id+"F0.wireOp",EDGE,"E34.3");Q39=makeQuery(id+"F0.imprint","IMPRINT",FACE,{"disambiguationData":[TD([[makeQuery(id+"F0.imprint","IMPRINT",EDGE,{"derivedFrom":subQ11}),-1.0]])]});}
            var Q40;
            {var subQ3=sQuery(id+"F0.wireOp",EDGE,"E54.top");var subQ5=sQuery(id+"F0.wireOp",EDGE,"E54.right");var subQ6=makeQuery(id+"F0.imprint","INTERSECT",VERTEX,{"derivedFrom":[subQ3,subQ5]});Q40=makeQuery(id+"F0.imprint","IMPRINT",FACE,{"disambiguationData":[TD([[makeQuery(id+"F0.imprint","IMPRINT",EDGE,{"disambiguationData":[TD([[subQ6,1.0]])],"derivedFrom":subQ3}),1.0]])]});}
            var Q41;
            {var subQ3=sQuery(id+"F0.wireOp",EDGE,"E54.bottom");var subQ5=sQuery(id+"F0.wireOp",EDGE,"E54.right");var subQ6=makeQuery(id+"F0.imprint","INTERSECT",VERTEX,{"derivedFrom":[subQ3,subQ5]});Q41=makeQuery(id+"F0.imprint","IMPRINT",FACE,{"disambiguationData":[TD([[makeQuery(id+"F0.imprint","IMPRINT",EDGE,{"disambiguationData":[TD([[subQ6,1.0]])],"derivedFrom":subQ3}),-1.0]])]});}
            var Q42;
            {var subQ3=sQuery(id+"F0.wireOp",EDGE,"E54.left");var subQ5=sQuery(id+"F0.wireOp",EDGE,"E54.bottom");var subQ7=makeQuery(id+"F0.imprint","INTERSECT",VERTEX,{"derivedFrom":[subQ5,subQ3]});Q42=makeQuery(id+"F0.imprint","IMPRINT",FACE,{"disambiguationData":[TD([[makeQuery(id+"F0.imprint","IMPRINT",EDGE,{"disambiguationData":[TD([[subQ7,-1.0]])],"derivedFrom":subQ5}),-1.0]])]});}
            var Q43;
            {var subQ3=sQuery(id+"F0.wireOp",EDGE,"E54.left");var subQ5=sQuery(id+"F0.wireOp",EDGE,"E54.top");var subQ7=makeQuery(id+"F0.imprint","INTERSECT",VERTEX,{"derivedFrom":[subQ5,subQ3]});Q43=makeQuery(id+"F0.imprint","IMPRINT",FACE,{"disambiguationData":[TD([[makeQuery(id+"F0.imprint","IMPRINT",EDGE,{"disambiguationData":[TD([[subQ7,-1.0]])],"derivedFrom":subQ5}),1.0]])]});}
            var Q44;
            Q44=makeQuery(id+"F0.imprint","IMPRINT",FACE,{"disambiguationData":[TD([[makeQuery(id+"F0.imprint","IMPRINT",EDGE,{"derivedFrom":sQuery(id+"F0.wireOp",EDGE,"fd3101a2-478a-4eb4-ba72-87674884c1bc.0")}),1.0]])]});
            var Q45;
            {var subQ0=sQuery(id+"F0.wireOp",EDGE,"E52.bottom");Q45=makeQuery(id+"F0.imprint","IMPRINT",FACE,{"disambiguationData":[TD([[makeQuery(id+"F0.imprint","IMPRINT",EDGE,{"derivedFrom":subQ0}),-1.0]])]});}
            var Q46;
            {var subQ1=sQuery(id+"F0.wireOp",EDGE,"E20.0");var subQ3=sQuery(id+"F0.wireOp",EDGE,"E52.left");var subQ4=makeQuery(id+"F0.imprint","INTERSECT",VERTEX,{"derivedFrom":[subQ1,subQ3]});Q46=makeQuery(id+"F0.imprint","IMPRINT",FACE,{"disambiguationData":[TD([[makeQuery(id+"F0.imprint","IMPRINT",EDGE,{"disambiguationData":[TD([[subQ4,1.0]])],"derivedFrom":subQ3}),1.0]])]});}
            var Q47;
            {var subQ0=sQuery(id+"F0.wireOp",EDGE,"E52.top");Q47=makeQuery(id+"F0.imprint","IMPRINT",FACE,{"disambiguationData":[TD([[makeQuery(id+"F0.imprint","IMPRINT",EDGE,{"derivedFrom":subQ0}),1.0]])]});}
            var Q48;
            {var subQ0=sQuery(id+"F0.wireOp",EDGE,"E52.top");Q48=makeQuery(id+"F0.imprint","IMPRINT",FACE,{"disambiguationData":[TD([[makeQuery(id+"F0.imprint","IMPRINT",EDGE,{"derivedFrom":subQ0}),1.0]])]});}
            var Q49;
            {var subQ1=sQuery(id+"F0.wireOp",EDGE,"E20.1");var subQ3=sQuery(id+"F0.wireOp",EDGE,"E52.right");var subQ4=makeQuery(id+"F0.imprint","INTERSECT",VERTEX,{"derivedFrom":[subQ1,subQ3]});Q49=makeQuery(id+"F0.imprint","IMPRINT",FACE,{"disambiguationData":[TD([[makeQuery(id+"F0.imprint","IMPRINT",EDGE,{"disambiguationData":[TD([[subQ4,1.0]])],"derivedFrom":subQ3}),-1.0]])]});}
            var Q50;
            {var subQ3=sQuery(id+"F0.wireOp",EDGE,"E57.right");var subQ5=sQuery(id+"F0.wireOp",EDGE,"E57.top");var subQ7=makeQuery(id+"F0.imprint","INTERSECT",VERTEX,{"derivedFrom":[subQ5,subQ3]});Q50=makeQuery(id+"F0.imprint","IMPRINT",FACE,{"disambiguationData":[TD([[makeQuery(id+"F0.imprint","IMPRINT",EDGE,{"disambiguationData":[TD([[subQ7,1.0]])],"derivedFrom":subQ5}),-1.0]])]});}
            var Q51;
            {var subQ3=sQuery(id+"F0.wireOp",EDGE,"E57.right");var subQ5=sQuery(id+"F0.wireOp",EDGE,"E57.bottom");var subQ7=makeQuery(id+"F0.imprint","INTERSECT",VERTEX,{"derivedFrom":[subQ5,subQ3]});Q51=makeQuery(id+"F0.imprint","IMPRINT",FACE,{"disambiguationData":[TD([[makeQuery(id+"F0.imprint","IMPRINT",EDGE,{"disambiguationData":[TD([[subQ7,1.0]])],"derivedFrom":subQ5}),1.0]])]});}
            var Q52;
            {var subQ3=sQuery(id+"F0.wireOp",EDGE,"E57.left");var subQ5=sQuery(id+"F0.wireOp",EDGE,"E57.bottom");var subQ6=makeQuery(id+"F0.imprint","INTERSECT",VERTEX,{"derivedFrom":[subQ5,subQ3]});Q52=makeQuery(id+"F0.imprint","IMPRINT",FACE,{"disambiguationData":[TD([[makeQuery(id+"F0.imprint","IMPRINT",EDGE,{"disambiguationData":[TD([[subQ6,-1.0]])],"derivedFrom":subQ5}),1.0]])]});}
            var Q53;
            {var subQ3=sQuery(id+"F0.wireOp",EDGE,"E57.top");var subQ5=sQuery(id+"F0.wireOp",EDGE,"E57.left");var subQ7=makeQuery(id+"F0.imprint","INTERSECT",VERTEX,{"derivedFrom":[subQ3,subQ5]});Q53=makeQuery(id+"F0.imprint","IMPRINT",FACE,{"disambiguationData":[TD([[makeQuery(id+"F0.imprint","IMPRINT",EDGE,{"disambiguationData":[TD([[subQ7,-1.0]])],"derivedFrom":subQ3}),-1.0]])]});}
            var Q54;
            {var subQ3=sQuery(id+"F0.wireOp",EDGE,"E48.left");var subQ5=sQuery(id+"F0.wireOp",EDGE,"E48.top");var subQ6=makeQuery(id+"F0.imprint","INTERSECT",VERTEX,{"derivedFrom":[subQ5,subQ3]});Q54=makeQuery(id+"F0.imprint","IMPRINT",FACE,{"disambiguationData":[TD([[makeQuery(id+"F0.imprint","IMPRINT",EDGE,{"disambiguationData":[TD([[subQ6,-1.0]])],"derivedFrom":subQ5}),1.0]])]});}
            var Q55;
            {var subQ3=sQuery(id+"F0.wireOp",EDGE,"E48.bottom");var subQ5=sQuery(id+"F0.wireOp",EDGE,"E48.left");var subQ6=makeQuery(id+"F0.imprint","INTERSECT",VERTEX,{"derivedFrom":[subQ3,subQ5]});Q55=makeQuery(id+"F0.imprint","IMPRINT",FACE,{"disambiguationData":[TD([[makeQuery(id+"F0.imprint","IMPRINT",EDGE,{"disambiguationData":[TD([[subQ6,-1.0]])],"derivedFrom":subQ3}),-1.0]])]});}
            var Q56;
            {var subQ3=sQuery(id+"F0.wireOp",EDGE,"E48.top");var subQ5=sQuery(id+"F0.wireOp",EDGE,"E48.right");var subQ7=makeQuery(id+"F0.imprint","INTERSECT",VERTEX,{"derivedFrom":[subQ3,subQ5]});Q56=makeQuery(id+"F0.imprint","IMPRINT",FACE,{"disambiguationData":[TD([[makeQuery(id+"F0.imprint","IMPRINT",EDGE,{"disambiguationData":[TD([[subQ7,1.0]])],"derivedFrom":subQ3}),1.0]])]});}
            var Q57;
            {var subQ3=sQuery(id+"F0.wireOp",EDGE,"E48.bottom");var subQ5=sQuery(id+"F0.wireOp",EDGE,"E48.right");var subQ7=makeQuery(id+"F0.imprint","INTERSECT",VERTEX,{"derivedFrom":[subQ3,subQ5]});Q57=makeQuery(id+"F0.imprint","IMPRINT",FACE,{"disambiguationData":[TD([[makeQuery(id+"F0.imprint","IMPRINT",EDGE,{"disambiguationData":[TD([[subQ7,1.0]])],"derivedFrom":subQ3}),-1.0]])]});}
            var Q58;
            {var subQ3=sQuery(id+"F0.wireOp",EDGE,"E68.left");var subQ5=sQuery(id+"F0.wireOp",EDGE,"E68.bottom");var subQ7=makeQuery(id+"F0.imprint","INTERSECT",VERTEX,{"derivedFrom":[subQ5,subQ3]});Q58=makeQuery(id+"F0.imprint","IMPRINT",FACE,{"disambiguationData":[TD([[makeQuery(id+"F0.imprint","IMPRINT",EDGE,{"disambiguationData":[TD([[subQ7,-1.0]])],"derivedFrom":subQ5}),1.0]])]});}
            var Q59;
            {var subQ3=sQuery(id+"F0.wireOp",EDGE,"E68.top");var subQ5=sQuery(id+"F0.wireOp",EDGE,"E68.left");var subQ7=makeQuery(id+"F0.imprint","INTERSECT",VERTEX,{"derivedFrom":[subQ3,subQ5]});Q59=makeQuery(id+"F0.imprint","IMPRINT",FACE,{"disambiguationData":[TD([[makeQuery(id+"F0.imprint","IMPRINT",EDGE,{"disambiguationData":[TD([[subQ7,-1.0]])],"derivedFrom":subQ3}),-1.0]])]});}
            var Q60;
            {var subQ3=sQuery(id+"F0.wireOp",EDGE,"E68.right");var subQ5=sQuery(id+"F0.wireOp",EDGE,"E68.bottom");var subQ7=makeQuery(id+"F0.imprint","INTERSECT",VERTEX,{"derivedFrom":[subQ5,subQ3]});Q60=makeQuery(id+"F0.imprint","IMPRINT",FACE,{"disambiguationData":[TD([[makeQuery(id+"F0.imprint","IMPRINT",EDGE,{"disambiguationData":[TD([[subQ7,1.0]])],"derivedFrom":subQ5}),1.0]])]});}
            var Q61;
            {var subQ3=sQuery(id+"F0.wireOp",EDGE,"E68.right");var subQ5=sQuery(id+"F0.wireOp",EDGE,"E68.top");var subQ6=makeQuery(id+"F0.imprint","INTERSECT",VERTEX,{"derivedFrom":[subQ5,subQ3]});Q61=makeQuery(id+"F0.imprint","IMPRINT",FACE,{"disambiguationData":[TD([[makeQuery(id+"F0.imprint","IMPRINT",EDGE,{"disambiguationData":[TD([[subQ6,1.0]])],"derivedFrom":subQ5}),-1.0]])]});}
            var Q62;
            Q62=makeQuery(id+"F0.imprint","IMPRINT",FACE,{"disambiguationData":[TD([[makeQuery(id+"F0.imprint","IMPRINT",EDGE,{"derivedFrom":sQuery(id+"F0.wireOp",EDGE,"E5.0")}),1.0]])]});
            var Q63;
            {var subQ0=sQuery(id+"F0.wireOp",EDGE,"E47.top");Q63=makeQuery(id+"F0.imprint","IMPRINT",FACE,{"disambiguationData":[TD([[makeQuery(id+"F0.imprint","IMPRINT",EDGE,{"derivedFrom":subQ0}),-1.0]])]});}
            var Q64;
            {var subQ1=sQuery(id+"F0.wireOp",EDGE,"E0.2");var subQ3=sQuery(id+"F0.wireOp",EDGE,"E47.right");var subQ4=makeQuery(id+"F0.imprint","INTERSECT",VERTEX,{"derivedFrom":[subQ1,subQ3]});Q64=makeQuery(id+"F0.imprint","IMPRINT",FACE,{"disambiguationData":[TD([[makeQuery(id+"F0.imprint","IMPRINT",EDGE,{"disambiguationData":[TD([[subQ4,-1.0]])],"derivedFrom":subQ3}),1.0]])]});}
            var Q65;
            {var subQ1=sQuery(id+"F0.wireOp",EDGE,"E0.1");var subQ3=sQuery(id+"F0.wireOp",EDGE,"E47.left");var subQ4=makeQuery(id+"F0.imprint","INTERSECT",VERTEX,{"derivedFrom":[subQ1,subQ3]});Q65=makeQuery(id+"F0.imprint","IMPRINT",FACE,{"disambiguationData":[TD([[makeQuery(id+"F0.imprint","IMPRINT",EDGE,{"disambiguationData":[TD([[subQ4,-1.0]])],"derivedFrom":subQ3}),-1.0]])]});}
            var Q66;
            {var subQ1=sQuery(id+"F0.wireOp",EDGE,"E47.bottom");Q66=makeQuery(id+"F0.imprint","IMPRINT",FACE,{"disambiguationData":[TD([[makeQuery(id+"F0.imprint","IMPRINT",EDGE,{"derivedFrom":subQ1}),1.0]])]});}
            var Q67;
            {var subQ3=sQuery(id+"F0.wireOp",EDGE,"E46.left");var subQ5=sQuery(id+"F0.wireOp",EDGE,"E46.bottom");var subQ7=makeQuery(id+"F0.imprint","INTERSECT",VERTEX,{"derivedFrom":[subQ5,subQ3]});Q67=makeQuery(id+"F0.imprint","IMPRINT",FACE,{"disambiguationData":[TD([[makeQuery(id+"F0.imprint","IMPRINT",EDGE,{"disambiguationData":[TD([[subQ7,-1.0]])],"derivedFrom":subQ5}),1.0]])]});}
            var Q68;
            {var subQ3=sQuery(id+"F0.wireOp",EDGE,"E46.left");var subQ5=sQuery(id+"F0.wireOp",EDGE,"E46.top");var subQ7=makeQuery(id+"F0.imprint","INTERSECT",VERTEX,{"derivedFrom":[subQ5,subQ3]});Q68=makeQuery(id+"F0.imprint","IMPRINT",FACE,{"disambiguationData":[TD([[makeQuery(id+"F0.imprint","IMPRINT",EDGE,{"disambiguationData":[TD([[subQ7,-1.0]])],"derivedFrom":subQ5}),-1.0]])]});}
            var Q69;
            {var subQ3=sQuery(id+"F0.wireOp",EDGE,"E46.right");var subQ5=sQuery(id+"F0.wireOp",EDGE,"E46.top");var subQ6=makeQuery(id+"F0.imprint","INTERSECT",VERTEX,{"derivedFrom":[subQ5,subQ3]});Q69=makeQuery(id+"F0.imprint","IMPRINT",FACE,{"disambiguationData":[TD([[makeQuery(id+"F0.imprint","IMPRINT",EDGE,{"disambiguationData":[TD([[subQ6,1.0]])],"derivedFrom":subQ5}),-1.0]])]});}
            var Q70;
            {var subQ3=sQuery(id+"F0.wireOp",EDGE,"E46.bottom");var subQ5=sQuery(id+"F0.wireOp",EDGE,"E46.right");var subQ7=makeQuery(id+"F0.imprint","INTERSECT",VERTEX,{"derivedFrom":[subQ3,subQ5]});Q70=makeQuery(id+"F0.imprint","IMPRINT",FACE,{"disambiguationData":[TD([[makeQuery(id+"F0.imprint","IMPRINT",EDGE,{"disambiguationData":[TD([[subQ7,1.0]])],"derivedFrom":subQ3}),1.0]])]});}
            var Q71;
            Q71=makeQuery(id+"F0.imprint","IMPRINT",FACE,{"disambiguationData":[TD([[makeQuery(id+"F0.imprint","IMPRINT",EDGE,{"derivedFrom":sQuery(id+"F0.wireOp",EDGE,"E9.0")}),1.0]])]});
            var Q72;
            {var subQ3=sQuery(id+"F0.wireOp",EDGE,"E67.bottom");var subQ5=sQuery(id+"F0.wireOp",EDGE,"E67.left");var subQ7=makeQuery(id+"F0.imprint","INTERSECT",VERTEX,{"derivedFrom":[subQ3,subQ5]});Q72=makeQuery(id+"F0.imprint","IMPRINT",FACE,{"disambiguationData":[TD([[makeQuery(id+"F0.imprint","IMPRINT",EDGE,{"disambiguationData":[TD([[subQ7,-1.0]])],"derivedFrom":subQ3}),-1.0]])]});}
            var Q73;
            {var subQ3=sQuery(id+"F0.wireOp",EDGE,"E67.right");var subQ5=sQuery(id+"F0.wireOp",EDGE,"E67.bottom");var subQ6=makeQuery(id+"F0.imprint","INTERSECT",VERTEX,{"derivedFrom":[subQ5,subQ3]});Q73=makeQuery(id+"F0.imprint","IMPRINT",FACE,{"disambiguationData":[TD([[makeQuery(id+"F0.imprint","IMPRINT",EDGE,{"disambiguationData":[TD([[subQ6,1.0]])],"derivedFrom":subQ5}),-1.0]])]});}
            var Q74;
            {var subQ3=sQuery(id+"F0.wireOp",EDGE,"E67.top");var subQ5=sQuery(id+"F0.wireOp",EDGE,"E67.right");var subQ7=makeQuery(id+"F0.imprint","INTERSECT",VERTEX,{"derivedFrom":[subQ3,subQ5]});Q74=makeQuery(id+"F0.imprint","IMPRINT",FACE,{"disambiguationData":[TD([[makeQuery(id+"F0.imprint","IMPRINT",EDGE,{"disambiguationData":[TD([[subQ7,1.0]])],"derivedFrom":subQ3}),1.0]])]});}
            var Q75;
            {var subQ3=sQuery(id+"F0.wireOp",EDGE,"E67.top");var subQ5=sQuery(id+"F0.wireOp",EDGE,"E67.left");var subQ6=makeQuery(id+"F0.imprint","INTERSECT",VERTEX,{"derivedFrom":[subQ3,subQ5]});Q75=makeQuery(id+"F0.imprint","IMPRINT",FACE,{"disambiguationData":[TD([[makeQuery(id+"F0.imprint","IMPRINT",EDGE,{"disambiguationData":[TD([[subQ6,-1.0]])],"derivedFrom":subQ3}),1.0]])]});}
            var Q76;
            {var subQ10=sQuery(id+"F0.wireOp",EDGE,"E38.3");Q76=makeQuery(id+"F0.imprint","IMPRINT",FACE,{"disambiguationData":[TD([[makeQuery(id+"F0.imprint","IMPRINT",EDGE,{"derivedFrom":subQ10}),-1.0]])]});}
            var Q77;
            {var subQ1=sQuery(id+"F0.wireOp",EDGE,"E58.top");Q77=makeQuery(id+"F0.imprint","IMPRINT",FACE,{"disambiguationData":[TD([[makeQuery(id+"F0.imprint","IMPRINT",EDGE,{"derivedFrom":subQ1}),-1.0]])]});}
            var Q78;
            {var subQ1=sQuery(id+"F0.wireOp",EDGE,"E21.5");var subQ3=sQuery(id+"F0.wireOp",EDGE,"E58.left");var subQ4=makeQuery(id+"F0.imprint","INTERSECT",VERTEX,{"derivedFrom":[subQ1,subQ3]});Q78=makeQuery(id+"F0.imprint","IMPRINT",FACE,{"disambiguationData":[TD([[makeQuery(id+"F0.imprint","IMPRINT",EDGE,{"disambiguationData":[TD([[subQ4,-1.0]])],"derivedFrom":subQ3}),-1.0]])]});}
            var Q79;
            {var subQ1=sQuery(id+"F0.wireOp",EDGE,"E58.bottom");Q79=makeQuery(id+"F0.imprint","IMPRINT",FACE,{"disambiguationData":[TD([[makeQuery(id+"F0.imprint","IMPRINT",EDGE,{"derivedFrom":subQ1}),1.0]])]});}
            var Q80;
            {var subQ1=sQuery(id+"F0.wireOp",EDGE,"E21.0");var subQ3=sQuery(id+"F0.wireOp",EDGE,"E58.right");var subQ4=makeQuery(id+"F0.imprint","INTERSECT",VERTEX,{"derivedFrom":[subQ1,subQ3]});Q80=makeQuery(id+"F0.imprint","IMPRINT",FACE,{"disambiguationData":[TD([[makeQuery(id+"F0.imprint","IMPRINT",EDGE,{"disambiguationData":[TD([[subQ4,-1.0]])],"derivedFrom":subQ3}),1.0]])]});}
            var Q81;
            {var subQ3=sQuery(id+"F0.wireOp",EDGE,"E69.top");var subQ5=sQuery(id+"F0.wireOp",EDGE,"E69.right");var subQ7=makeQuery(id+"F0.imprint","INTERSECT",VERTEX,{"derivedFrom":[subQ3,subQ5]});Q81=makeQuery(id+"F0.imprint","IMPRINT",FACE,{"disambiguationData":[TD([[makeQuery(id+"F0.imprint","IMPRINT",EDGE,{"disambiguationData":[TD([[subQ7,1.0]])],"derivedFrom":subQ3}),1.0]])]});}
            var Q82;
            {var subQ3=sQuery(id+"F0.wireOp",EDGE,"E69.bottom");var subQ5=sQuery(id+"F0.wireOp",EDGE,"E69.right");var subQ7=makeQuery(id+"F0.imprint","INTERSECT",VERTEX,{"derivedFrom":[subQ3,subQ5]});Q82=makeQuery(id+"F0.imprint","IMPRINT",FACE,{"disambiguationData":[TD([[makeQuery(id+"F0.imprint","IMPRINT",EDGE,{"disambiguationData":[TD([[subQ7,1.0]])],"derivedFrom":subQ3}),-1.0]])]});}
            var Q83;
            {var subQ3=sQuery(id+"F0.wireOp",EDGE,"E69.left");var subQ5=sQuery(id+"F0.wireOp",EDGE,"E69.bottom");var subQ7=makeQuery(id+"F0.imprint","INTERSECT",VERTEX,{"derivedFrom":[subQ5,subQ3]});Q83=makeQuery(id+"F0.imprint","IMPRINT",FACE,{"disambiguationData":[TD([[makeQuery(id+"F0.imprint","IMPRINT",EDGE,{"disambiguationData":[TD([[subQ7,-1.0]])],"derivedFrom":subQ5}),-1.0]])]});}
            var Q84;
            {var subQ3=sQuery(id+"F0.wireOp",EDGE,"E69.left");var subQ5=sQuery(id+"F0.wireOp",EDGE,"E69.top");var subQ7=makeQuery(id+"F0.imprint","INTERSECT",VERTEX,{"derivedFrom":[subQ5,subQ3]});Q84=makeQuery(id+"F0.imprint","IMPRINT",FACE,{"disambiguationData":[TD([[makeQuery(id+"F0.imprint","IMPRINT",EDGE,{"disambiguationData":[TD([[subQ7,-1.0]])],"derivedFrom":subQ5}),1.0]])]});}
            var Q85;
            {var subQ3=sQuery(id+"F0.wireOp",EDGE,"E66.left");var subQ5=sQuery(id+"F0.wireOp",EDGE,"E66.bottom");var subQ6=makeQuery(id+"F0.imprint","INTERSECT",VERTEX,{"derivedFrom":[subQ5,subQ3]});Q85=makeQuery(id+"F0.imprint","IMPRINT",FACE,{"disambiguationData":[TD([[makeQuery(id+"F0.imprint","IMPRINT",EDGE,{"disambiguationData":[TD([[subQ6,-1.0]])],"derivedFrom":subQ5}),1.0]])]});}
            var Q86;
            {var subQ3=sQuery(id+"F0.wireOp",EDGE,"E66.left");var subQ5=sQuery(id+"F0.wireOp",EDGE,"E66.top");var subQ6=makeQuery(id+"F0.imprint","INTERSECT",VERTEX,{"derivedFrom":[subQ5,subQ3]});Q86=makeQuery(id+"F0.imprint","IMPRINT",FACE,{"disambiguationData":[TD([[makeQuery(id+"F0.imprint","IMPRINT",EDGE,{"disambiguationData":[TD([[subQ6,-1.0]])],"derivedFrom":subQ5}),-1.0]])]});}
            var Q87;
            {var subQ3=sQuery(id+"F0.wireOp",EDGE,"E66.right");var subQ5=sQuery(id+"F0.wireOp",EDGE,"E66.top");var subQ6=makeQuery(id+"F0.imprint","INTERSECT",VERTEX,{"derivedFrom":[subQ5,subQ3]});Q87=makeQuery(id+"F0.imprint","IMPRINT",FACE,{"disambiguationData":[TD([[makeQuery(id+"F0.imprint","IMPRINT",EDGE,{"disambiguationData":[TD([[subQ6,1.0]])],"derivedFrom":subQ5}),-1.0]])]});}
            var Q88;
            {var subQ3=sQuery(id+"F0.wireOp",EDGE,"E66.bottom");var subQ5=sQuery(id+"F0.wireOp",EDGE,"E66.right");var subQ6=makeQuery(id+"F0.imprint","INTERSECT",VERTEX,{"derivedFrom":[subQ3,subQ5]});Q88=makeQuery(id+"F0.imprint","IMPRINT",FACE,{"disambiguationData":[TD([[makeQuery(id+"F0.imprint","IMPRINT",EDGE,{"disambiguationData":[TD([[subQ6,1.0]])],"derivedFrom":subQ3}),1.0]])]});}
            var Q89;
            {var subQ10=sQuery(id+"F0.wireOp",EDGE,"E42.3");Q89=makeQuery(id+"F0.imprint","IMPRINT",FACE,{"disambiguationData":[TD([[makeQuery(id+"F0.imprint","IMPRINT",EDGE,{"derivedFrom":subQ10}),-1.0]])]});}
            var Q90;
            {var subQ1=sQuery(id+"F0.wireOp",EDGE,"E59.top");Q90=makeQuery(id+"F0.imprint","IMPRINT",FACE,{"disambiguationData":[TD([[makeQuery(id+"F0.imprint","IMPRINT",EDGE,{"derivedFrom":subQ1}),-1.0]])]});}
            var Q91;
            {var subQ1=sQuery(id+"F0.wireOp",EDGE,"E8.5");var subQ3=sQuery(id+"F0.wireOp",EDGE,"E59.left");var subQ4=makeQuery(id+"F0.imprint","INTERSECT",VERTEX,{"derivedFrom":[subQ1,subQ3]});Q91=makeQuery(id+"F0.imprint","IMPRINT",FACE,{"disambiguationData":[TD([[makeQuery(id+"F0.imprint","IMPRINT",EDGE,{"disambiguationData":[TD([[subQ4,-1.0]])],"derivedFrom":subQ3}),-1.0]])]});}
            var Q92;
            {var subQ1=sQuery(id+"F0.wireOp",EDGE,"E59.bottom");Q92=makeQuery(id+"F0.imprint","IMPRINT",FACE,{"disambiguationData":[TD([[makeQuery(id+"F0.imprint","IMPRINT",EDGE,{"derivedFrom":subQ1}),1.0]])]});}
            var Q93;
            {var subQ1=sQuery(id+"F0.wireOp",EDGE,"E8.0");var subQ3=sQuery(id+"F0.wireOp",EDGE,"E59.right");var subQ4=makeQuery(id+"F0.imprint","INTERSECT",VERTEX,{"derivedFrom":[subQ1,subQ3]});Q93=makeQuery(id+"F0.imprint","IMPRINT",FACE,{"disambiguationData":[TD([[makeQuery(id+"F0.imprint","IMPRINT",EDGE,{"disambiguationData":[TD([[subQ4,-1.0]])],"derivedFrom":subQ3}),1.0]])]});}
            var Q94;
            {var subQ3=sQuery(id+"F0.wireOp",EDGE,"E60.bottom");var subQ5=sQuery(id+"F0.wireOp",EDGE,"E60.left");var subQ6=makeQuery(id+"F0.imprint","INTERSECT",VERTEX,{"derivedFrom":[subQ3,subQ5]});Q94=makeQuery(id+"F0.imprint","IMPRINT",FACE,{"disambiguationData":[TD([[makeQuery(id+"F0.imprint","IMPRINT",EDGE,{"disambiguationData":[TD([[subQ6,-1.0]])],"derivedFrom":subQ3}),-1.0]])]});}
            var Q95;
            {var subQ3=sQuery(id+"F0.wireOp",EDGE,"E60.bottom");var subQ5=sQuery(id+"F0.wireOp",EDGE,"E60.right");var subQ7=makeQuery(id+"F0.imprint","INTERSECT",VERTEX,{"derivedFrom":[subQ3,subQ5]});Q95=makeQuery(id+"F0.imprint","IMPRINT",FACE,{"disambiguationData":[TD([[makeQuery(id+"F0.imprint","IMPRINT",EDGE,{"disambiguationData":[TD([[subQ7,1.0]])],"derivedFrom":subQ3}),-1.0]])]});}
            var Q96;
            {var subQ3=sQuery(id+"F0.wireOp",EDGE,"E60.top");var subQ5=sQuery(id+"F0.wireOp",EDGE,"E60.right");var subQ7=makeQuery(id+"F0.imprint","INTERSECT",VERTEX,{"derivedFrom":[subQ3,subQ5]});Q96=makeQuery(id+"F0.imprint","IMPRINT",FACE,{"disambiguationData":[TD([[makeQuery(id+"F0.imprint","IMPRINT",EDGE,{"disambiguationData":[TD([[subQ7,1.0]])],"derivedFrom":subQ3}),1.0]])]});}
            var Q97;
            {var subQ3=sQuery(id+"F0.wireOp",EDGE,"E60.left");var subQ5=sQuery(id+"F0.wireOp",EDGE,"E60.top");var subQ7=makeQuery(id+"F0.imprint","INTERSECT",VERTEX,{"derivedFrom":[subQ5,subQ3]});Q97=makeQuery(id+"F0.imprint","IMPRINT",FACE,{"disambiguationData":[TD([[makeQuery(id+"F0.imprint","IMPRINT",EDGE,{"disambiguationData":[TD([[subQ7,-1.0]])],"derivedFrom":subQ5}),1.0]])]});}
            var Q98;
            {var subQ14=sQuery(id+"F0.wireOp",EDGE,"E22.3");Q98=makeQuery(id+"F0.imprint","IMPRINT",FACE,{"disambiguationData":[TD([[makeQuery(id+"F0.imprint","IMPRINT",EDGE,{"derivedFrom":subQ14}),-1.0]])]});}
            var Q99;
            {var subQ1=sQuery(id+"F0.wireOp",EDGE,"E56.top");Q99=makeQuery(id+"F0.imprint","IMPRINT",FACE,{"disambiguationData":[TD([[makeQuery(id+"F0.imprint","IMPRINT",EDGE,{"derivedFrom":subQ1}),-1.0]])]});}
            var Q100;
            {var subQ1=sQuery(id+"F0.wireOp",EDGE,"E56.bottom");Q100=makeQuery(id+"F0.imprint","IMPRINT",FACE,{"disambiguationData":[TD([[makeQuery(id+"F0.imprint","IMPRINT",EDGE,{"derivedFrom":subQ1}),1.0]])]});}
            var Q101;
            {var subQ1=sQuery(id+"F0.wireOp",EDGE,"E8.3");var subQ3=sQuery(id+"F0.wireOp",EDGE,"E56.left");var subQ4=makeQuery(id+"F0.imprint","INTERSECT",VERTEX,{"derivedFrom":[subQ1,subQ3]});Q101=makeQuery(id+"F0.imprint","IMPRINT",FACE,{"disambiguationData":[TD([[makeQuery(id+"F0.imprint","IMPRINT",EDGE,{"disambiguationData":[TD([[subQ4,1.0]])],"derivedFrom":subQ3}),-1.0]])]});}
            var Q102;
            {var subQ1=sQuery(id+"F0.wireOp",EDGE,"E8.2");var subQ3=sQuery(id+"F0.wireOp",EDGE,"E56.right");var subQ4=makeQuery(id+"F0.imprint","INTERSECT",VERTEX,{"derivedFrom":[subQ1,subQ3]});Q102=makeQuery(id+"F0.imprint","IMPRINT",FACE,{"disambiguationData":[TD([[makeQuery(id+"F0.imprint","IMPRINT",EDGE,{"disambiguationData":[TD([[subQ4,1.0]])],"derivedFrom":subQ3}),1.0]])]});}
            var Q103;
            {var subQ3=sQuery(id+"F0.wireOp",EDGE,"E61.left");var subQ5=sQuery(id+"F0.wireOp",EDGE,"E61.top");var subQ7=makeQuery(id+"F0.imprint","INTERSECT",VERTEX,{"derivedFrom":[subQ5,subQ3]});Q103=makeQuery(id+"F0.imprint","IMPRINT",FACE,{"disambiguationData":[TD([[makeQuery(id+"F0.imprint","IMPRINT",EDGE,{"disambiguationData":[TD([[subQ7,-1.0]])],"derivedFrom":subQ5}),-1.0]])]});}
            var Q104;
            {var subQ3=sQuery(id+"F0.wireOp",EDGE,"E61.bottom");var subQ5=sQuery(id+"F0.wireOp",EDGE,"E61.left");var subQ7=makeQuery(id+"F0.imprint","INTERSECT",VERTEX,{"derivedFrom":[subQ3,subQ5]});Q104=makeQuery(id+"F0.imprint","IMPRINT",FACE,{"disambiguationData":[TD([[makeQuery(id+"F0.imprint","IMPRINT",EDGE,{"disambiguationData":[TD([[subQ7,-1.0]])],"derivedFrom":subQ3}),1.0]])]});}
            var Q105;
            {var subQ3=sQuery(id+"F0.wireOp",EDGE,"E61.bottom");var subQ5=sQuery(id+"F0.wireOp",EDGE,"E61.right");var subQ6=makeQuery(id+"F0.imprint","INTERSECT",VERTEX,{"derivedFrom":[subQ3,subQ5]});Q105=makeQuery(id+"F0.imprint","IMPRINT",FACE,{"disambiguationData":[TD([[makeQuery(id+"F0.imprint","IMPRINT",EDGE,{"disambiguationData":[TD([[subQ6,1.0]])],"derivedFrom":subQ3}),1.0]])]});}
            var Q106;
            {var subQ3=sQuery(id+"F0.wireOp",EDGE,"E61.right");var subQ5=sQuery(id+"F0.wireOp",EDGE,"E61.top");var subQ7=makeQuery(id+"F0.imprint","INTERSECT",VERTEX,{"derivedFrom":[subQ5,subQ3]});Q106=makeQuery(id+"F0.imprint","IMPRINT",FACE,{"disambiguationData":[TD([[makeQuery(id+"F0.imprint","IMPRINT",EDGE,{"disambiguationData":[TD([[subQ7,1.0]])],"derivedFrom":subQ5}),-1.0]])]});}
            var Q107;
            {var subQ3=sQuery(id+"F0.wireOp",EDGE,"E63.bottom");var subQ5=sQuery(id+"F0.wireOp",EDGE,"E63.left");var subQ6=makeQuery(id+"F0.imprint","INTERSECT",VERTEX,{"derivedFrom":[subQ3,subQ5]});Q107=makeQuery(id+"F0.imprint","IMPRINT",FACE,{"disambiguationData":[TD([[makeQuery(id+"F0.imprint","IMPRINT",EDGE,{"disambiguationData":[TD([[subQ6,-1.0]])],"derivedFrom":subQ3}),-1.0]])]});}
            var Q108;
            {var subQ3=sQuery(id+"F0.wireOp",EDGE,"E63.right");var subQ5=sQuery(id+"F0.wireOp",EDGE,"E63.bottom");var subQ7=makeQuery(id+"F0.imprint","INTERSECT",VERTEX,{"derivedFrom":[subQ5,subQ3]});Q108=makeQuery(id+"F0.imprint","IMPRINT",FACE,{"disambiguationData":[TD([[makeQuery(id+"F0.imprint","IMPRINT",EDGE,{"disambiguationData":[TD([[subQ7,1.0]])],"derivedFrom":subQ5}),-1.0]])]});}
            var Q109;
            {var subQ3=sQuery(id+"F0.wireOp",EDGE,"E63.top");var subQ5=sQuery(id+"F0.wireOp",EDGE,"E63.left");var subQ6=makeQuery(id+"F0.imprint","INTERSECT",VERTEX,{"derivedFrom":[subQ3,subQ5]});Q109=makeQuery(id+"F0.imprint","IMPRINT",FACE,{"disambiguationData":[TD([[makeQuery(id+"F0.imprint","IMPRINT",EDGE,{"disambiguationData":[TD([[subQ6,-1.0]])],"derivedFrom":subQ3}),1.0]])]});}
            var Q110;
            {var subQ3=sQuery(id+"F0.wireOp",EDGE,"E63.right");var subQ5=sQuery(id+"F0.wireOp",EDGE,"E63.top");var subQ7=makeQuery(id+"F0.imprint","INTERSECT",VERTEX,{"derivedFrom":[subQ5,subQ3]});Q110=makeQuery(id+"F0.imprint","IMPRINT",FACE,{"disambiguationData":[TD([[makeQuery(id+"F0.imprint","IMPRINT",EDGE,{"disambiguationData":[TD([[subQ7,1.0]])],"derivedFrom":subQ5}),1.0]])]});}
            var Q111;
            {var subQ24=sQuery(id+"F0.wireOp",EDGE,"E52.top");Q111=makeQuery(id+"F0.imprint","IMPRINT",FACE,{"disambiguationData":[TD([[makeQuery(id+"F0.imprint","IMPRINT",EDGE,{"derivedFrom":subQ24}),-1.0]])]});}
            var Q112;
            {var subQ17=sQuery(id+"F0.wireOp",EDGE,"E52.bottom");Q112=makeQuery(id+"F0.imprint","IMPRINT",FACE,{"disambiguationData":[TD([[makeQuery(id+"F0.imprint","IMPRINT",EDGE,{"derivedFrom":subQ17}),1.0]])]});}
            extrude(context, id + "F1", {"entities" : qUnion([Q0, Q1, Q2, Q3, Q4, Q5, Q6, Q7, Q8, Q9, Q10, Q11, Q12, Q13, Q14, Q15, Q16, Q17, Q18, Q19, Q20, Q21, Q22, Q23, Q24, Q25, Q26, Q27, Q28, Q29, Q30, Q31, Q32, Q33, Q34, Q35, Q36, Q37, Q38, Q39, Q40, Q41, Q42, Q43, Q44, Q45, Q46, Q47, Q48, Q49, Q50, Q51, Q52, Q53, Q54, Q55, Q56, Q57, Q58, Q59, Q60, Q61, Q62, Q63, Q64, Q65, Q66, Q67, Q68, Q69, Q70, Q71, Q72, Q73, Q74, Q75, Q76, Q77, Q78, Q79, Q80, Q81, Q82, Q83, Q84, Q85, Q86, Q87, Q88, Q89, Q90, Q91, Q92, Q93, Q94, Q95, Q96, Q97, Q98, Q99, Q100, Q101, Q102, Q103, Q104, Q105, Q106, Q107, Q108, Q109, Q110, Q111, Q112]), "endBound" : BoundingType.SYMMETRIC, "oppositeDirection" : true, "depth" : 5 * mm, "offsetDistance" : 25 * mm});
        }
        {
            var Q0;
            {var subQ8=sQuery(id+"F0.wireOp",EDGE,"E62.left");var subQ13=sQuery(id+"F0.wireOp",EDGE,"E12.2");var subQ14=makeQuery(id+"F0.imprint","INTERSECT",VERTEX,{"derivedFrom":[subQ13,subQ8]});Q0=makeQuery(id+"F0.imprint","IMPRINT",FACE,{"disambiguationData":[TD([[makeQuery(id+"F0.imprint","IMPRINT",EDGE,{"disambiguationData":[TD([[subQ14,-1.0]])],"derivedFrom":subQ13}),1.0]])]});}
            var Q1;
            {var subQ3=sQuery(id+"F0.wireOp",EDGE,"E16.2");var subQ13=sQuery(id+"F0.wireOp",EDGE,"E64.top");var subQ14=makeQuery(id+"F0.imprint","INTERSECT",VERTEX,{"derivedFrom":[subQ3,subQ13]});Q1=makeQuery(id+"F0.imprint","IMPRINT",FACE,{"disambiguationData":[TD([[makeQuery(id+"F0.imprint","IMPRINT",EDGE,{"disambiguationData":[TD([[subQ14,-1.0]])],"derivedFrom":subQ3}),1.0]])]});}
            var Q2;
            {var subQ10=sQuery(id+"F0.wireOp",EDGE,"E20.0");var subQ12=sQuery(id+"F0.wireOp",EDGE,"E54.left");var subQ13=makeQuery(id+"F0.imprint","INTERSECT",VERTEX,{"derivedFrom":[subQ10,subQ12]});Q2=makeQuery(id+"F0.imprint","IMPRINT",FACE,{"disambiguationData":[TD([[makeQuery(id+"F0.imprint","IMPRINT",EDGE,{"disambiguationData":[TD([[subQ13,-1.0]])],"derivedFrom":subQ10}),1.0]])]});}
            var Q3;
            {var subQ11=sQuery(id+"F0.wireOp",EDGE,"E68.top");var subQ12=sQuery(id+"F0.wireOp",EDGE,"E4.5");var subQ13=makeQuery(id+"F0.imprint","INTERSECT",VERTEX,{"derivedFrom":[subQ12,subQ11]});Q3=makeQuery(id+"F0.imprint","IMPRINT",FACE,{"disambiguationData":[TD([[makeQuery(id+"F0.imprint","IMPRINT",EDGE,{"disambiguationData":[TD([[subQ13,-1.0]])],"derivedFrom":subQ12}),1.0]])]});}
            var Q4;
            {var subQ7=sQuery(id+"F0.wireOp",EDGE,"E66.bottom");var subQ8=sQuery(id+"F0.wireOp",EDGE,"E4.2");var subQ9=makeQuery(id+"F0.imprint","INTERSECT",VERTEX,{"derivedFrom":[subQ8,subQ7]});Q4=makeQuery(id+"F0.imprint","IMPRINT",FACE,{"disambiguationData":[TD([[makeQuery(id+"F0.imprint","IMPRINT",EDGE,{"disambiguationData":[TD([[subQ9,-1.0]])],"derivedFrom":subQ8}),1.0]])]});}
            var Q5;
            {var subQ1=sQuery(id+"F0.wireOp",EDGE,"E8.2");var subQ12=sQuery(id+"F0.wireOp",EDGE,"E60.left");var subQ13=makeQuery(id+"F0.imprint","INTERSECT",VERTEX,{"derivedFrom":[subQ1,subQ12]});Q5=makeQuery(id+"F0.imprint","IMPRINT",FACE,{"disambiguationData":[TD([[makeQuery(id+"F0.imprint","IMPRINT",EDGE,{"disambiguationData":[TD([[subQ13,-1.0]])],"derivedFrom":subQ1}),1.0]])]});}
            extrude(context, id + "F2", {"entities" : qUnion([Q0, Q1, Q2, Q3, Q4, Q5]), "depth" : 15 * mm, "offsetDistance" : 25 * mm, "hasSecondDirection" : true, "secondDirectionOppositeDirection" : true, "secondDirectionDepth" : 2 * mm});
        }
        {
            var Q0;
            Q0=makeQuery(id+"F1.opExtrude","CAP_FACE",FACE,{"disambiguationData":[OSD([sQuery(id+"F0.wireOp",EDGE,"E0.0"),sQuery(id+"F0.wireOp",EDGE,"E0.1"),sQuery(id+"F0.wireOp",EDGE,"E0.2"),sQuery(id+"F0.wireOp",EDGE,"E0.3"),sQuery(id+"F0.wireOp",EDGE,"E0.4"),sQuery(id+"F0.wireOp",EDGE,"E0.5"),sQuery(id+"F0.wireOp",EDGE,"E1.0"),sQuery(id+"F0.wireOp",EDGE,"E1.1"),sQuery(id+"F0.wireOp",EDGE,"E1.2"),sQuery(id+"F0.wireOp",EDGE,"E1.3"),sQuery(id+"F0.wireOp",EDGE,"E2"),sQuery(id+"F0.wireOp",EDGE,"E3")])],"isStart":true});
            var sketch = newSketch(context, id + "F3", { "sketchPlane" : qUnion([Q0])});
            skText(sketch, "E77", { "text": "2017", "fontName": "OpenSans-Bold.ttf"});
            skText(sketch, "E78", { "text": "v1", "fontName": "OpenSans-Regular.ttf"});
            const initialGuessF3  = {"E77": [0, 0.00961, 0.5, -0.86603, 0.00518], "E78": [0.0088, 0.00683, 0.5, -0.86603, 0.00236]};
            skSetInitialGuess(sketch, initialGuessF3);
            skSolve(sketch);
        }
        {
            var Q0;
            Q0 = qSketchRegion(id + "F3", true);
            extrude(context, id + "F4", {"entities" : qUnion([Q0]), "operationType" : NewBodyOperationType.REMOVE, "oppositeDirection" : true, "depth" : 1 * mm, "offsetDistance" : 25 * mm});
        }
    });
